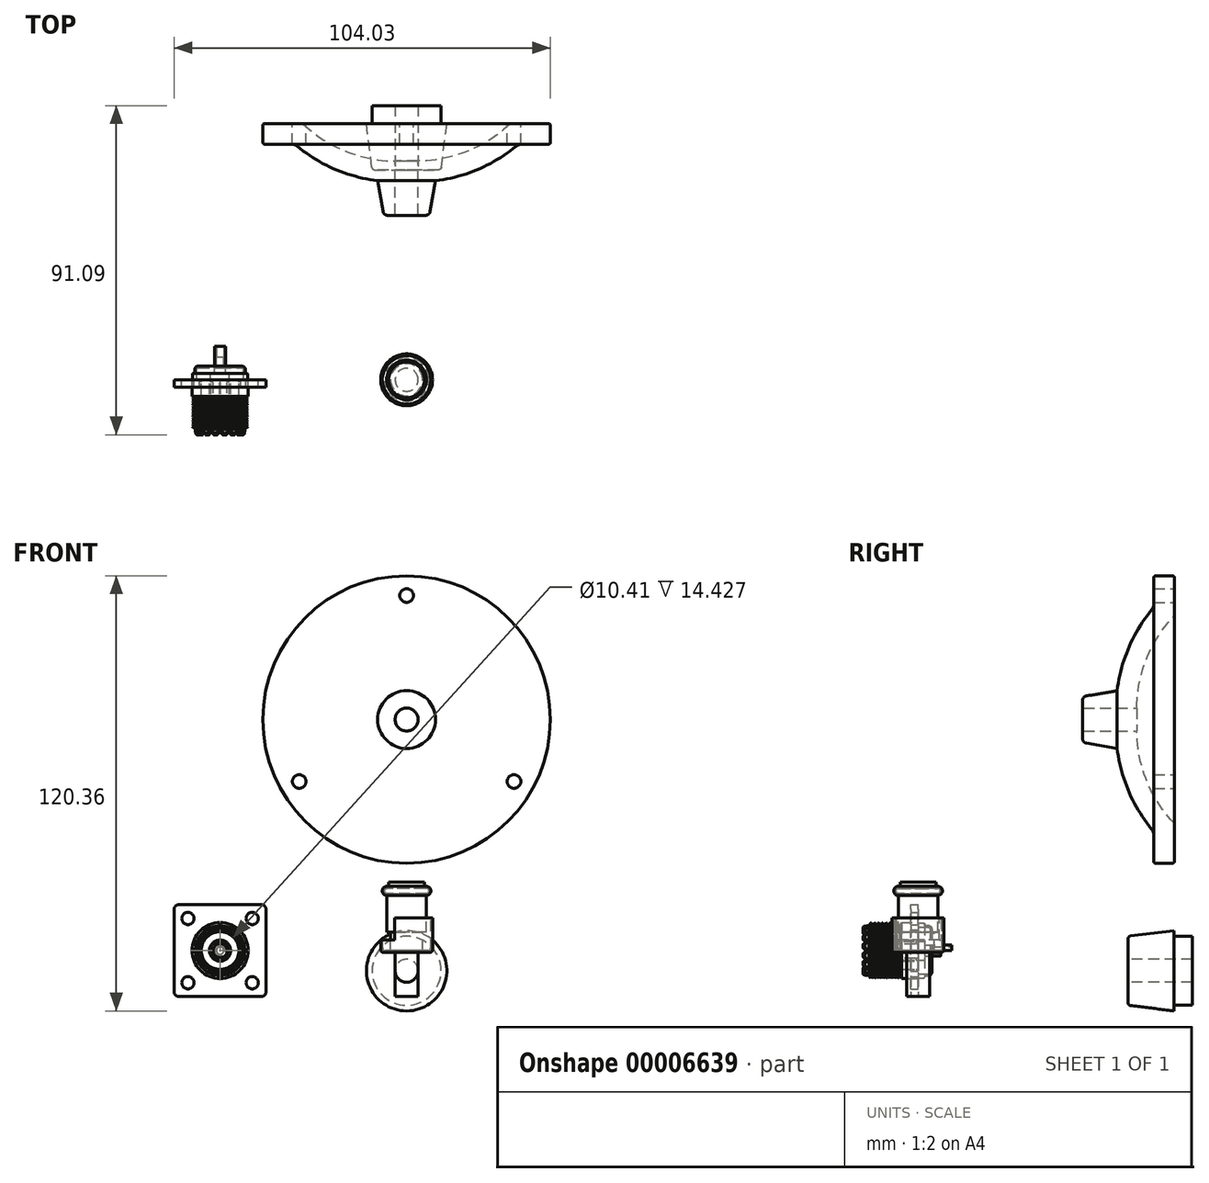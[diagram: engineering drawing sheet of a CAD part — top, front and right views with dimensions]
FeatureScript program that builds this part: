
annotation { "Feature Type Name" : "Feature", "Feature Type Description" : "" }
export const myFeature = defineFeature(function(context is Context, id is Id, definition is map)
    precondition{}
    {
        {
            var Q0;
            Q0=qCreatedBy(makeId("Right.planeOp"),FACE);
            var sketch = newSketch(context, id + "F0", { "sketchPlane" : qUnion([Q0])});
            skLineSegment(sketch, "E0", {"start": v(70.89, 103.16) * mm, "end": v(70.89, 92.87) * mm});
            skLineSegment(sketch, "E1", {"start": v(65.17, 103.16) * mm, "end": v(65.17, 84.88) * mm});
            skLineSegment(sketch, "E2", {"start": v(69.81, 63.92) * mm, "end": v(49.64, 63.92) * mm, "construction": true});
            skLineSegment(sketch, "E3", {"start": v(86.2, 94.9) * mm, "end": v(31.84, 94.9) * mm, "construction": true});
            skLineSegment(sketch, "E4", {"start": v(70.38, 103.67) * mm, "end": v(65.68, 103.67) * mm});
            skLineSegment(sketch, "E5", {"start": v(54.76, 115.1) * mm, "end": v(54.76, 52.48) * mm, "construction": true});
            skLineSegment(sketch, "E6", {"start": v(45.49, 106.52) * mm, "end": v(45.49, 54.26) * mm, "construction": true});
            skLineSegment(sketch, "E7", {"start": v(78.6, 71.85) * mm, "end": v(34.43, 71.85) * mm, "construction": true});
            skLineSegment(sketch, "E8", {"start": v(27.47, 70.27) * mm, "end": v(90.57, 70.27) * mm, "construction": true});
            skLineSegment(sketch, "E9", {"start": v(86.85, 67.1) * mm, "end": v(33.78, 67.1) * mm, "construction": true});
            skPoint(sketch, "E10.orphan", {"position": v(70.89, 63.92) * mm});
            skLineSegment(sketch, "E11", {"start": v(60.5, 67.1) * mm, "end": v(45.74, 67.1) * mm});
            skLineSegment(sketch, "E12", {"start": v(45.49, 67.34) * mm, "end": v(45.49, 69.2) * mm});
            skLineSegment(sketch, "E13", {"start": v(46.54, 70.45) * mm, "end": v(55.07, 71.9) * mm});
            skArc(sketch, "E14", {"start": v(65.17, 94.9) * mm, "mid": v(58.4, 84.13) * mm, "end": v(55.06, 71.85) * mm});
            skArc(sketch, "E15.0", {"start": v(70.75, 92.52) * mm, "mid": v(63.21, 80.75) * mm, "end": v(60.5, 67.04) * mm});
            skPoint(sketch, "E16.visualSharp", {"position": v(70.89, 103.67) * mm});
            skArc(sketch, "E16.filletArc", {"start": v(70.89, 103.16) * mm, "mid": v(70.74, 103.52) * mm, "end": v(70.38, 103.67) * mm});
            skPoint(sketch, "E17.visualSharp", {"position": v(65.17, 103.67) * mm});
            skArc(sketch, "E17.filletArc", {"start": v(65.68, 103.67) * mm, "mid": v(65.32, 103.52) * mm, "end": v(65.17, 103.16) * mm});
            skPoint(sketch, "E18.visualSharp", {"position": v(70.89, 92.67) * mm});
            skArc(sketch, "E18.filletArc", {"start": v(70.75, 92.52) * mm, "mid": v(70.85, 92.68) * mm, "end": v(70.89, 92.87) * mm});
            skPoint(sketch, "E19.visualSharp", {"position": v(45.49, 70.27) * mm});
            skArc(sketch, "E19.filletArc", {"start": v(46.54, 70.45) * mm, "mid": v(45.79, 70.01) * mm, "end": v(45.49, 69.2) * mm});
            skPoint(sketch, "E20.visualSharp", {"position": v(45.49, 67.1) * mm});
            skArc(sketch, "E20.filletArc", {"start": v(45.49, 67.34) * mm, "mid": v(45.56, 67.17) * mm, "end": v(45.74, 67.1) * mm});
            skLineSegment(sketch, "E21", {"start": v(43.2, -5.58) * mm, "end": v(88.96, -5.58) * mm, "construction": true});
            skLineSegment(sketch, "E22", {"start": v(70.77, -33.7) * mm, "end": v(70.77, 20.3) * mm, "construction": true});
            skLineSegment(sketch, "E23", {"start": v(75.85, -2.4) * mm, "end": v(58.07, -2.4) * mm});
            skLineSegment(sketch, "E24", {"start": v(58.07, -2.4) * mm, "end": v(58.07, 3.27) * mm});
            skLineSegment(sketch, "E25", {"start": v(58.74, 4.03) * mm, "end": v(70.77, 5.53) * mm});
            skLineSegment(sketch, "E26", {"start": v(70.77, 5.53) * mm, "end": v(70.77, 3.95) * mm});
            skLineSegment(sketch, "E27", {"start": v(70.77, 3.95) * mm, "end": v(75.85, 3.95) * mm});
            skLineSegment(sketch, "E28", {"start": v(75.85, 3.95) * mm, "end": v(75.85, -2.4) * mm});
            skPoint(sketch, "E29.visualSharp", {"position": v(58.07, 3.95) * mm});
            skArc(sketch, "E29.filletArc", {"start": v(58.74, 4.03) * mm, "mid": v(58.26, 3.78) * mm, "end": v(58.07, 3.27) * mm});
            skSolve(sketch);
        }
        {
            var Q0;
            Q0=makeQuery(id+"F0.imprint","IMPRINT",FACE,{"disambiguationData":[TD([[makeQuery(id+"F0.imprint","IMPRINT",EDGE,{"derivedFrom":sQuery(id+"F0.wireOp",EDGE,"E0")}),-1.0]])]});
            var Q1;
            {var subQ1=sQuery(id+"F0.wireOp",EDGE,"E11");Q1=makeQuery(id+"F0.imprint","IMPRINT",FACE,{"disambiguationData":[TD([[makeQuery(id+"F0.imprint","IMPRINT",EDGE,{"derivedFrom":subQ1}),-1.0]])]});}
            var Q2;
            Q2=sQuery(id+"F0.wireOp",EDGE,"E2");
            revolve(context, id + "F1", {"entities" : qUnion([Q0, Q1]), "axis" : qUnion([Q2]), "revolveType" : RevolveType.FULL});
        }
        {
            var Q0;
            Q0=makeQuery(id+"F1.opRevolve","SWEPT_EDGE",EDGE,{"disambiguationData":[OSD([sQuery(id+"F0.wireOp",EDGE,"E1"),sQuery(id+"F0.wireOp",EDGE,"E14")])]});
            fillet(context, id + "F2", {"entities" : qUnion([Q0]), "radius" : 2.54 * mm, "tangentPropagation" : true, "allowEdgeOverflow" : false});
        }
        {
            var Q0;
            Q0=makeQuery(id+"F1.opRevolve","SWEPT_FACE",FACE,{"disambiguationData":[OSD([sQuery(id+"F0.wireOp",EDGE,"E0")])]});
            var sketch = newSketch(context, id + "F3", { "sketchPlane" : qUnion([Q0])});
            skLineSegment(sketch, "E30", {"start": v(0, 63.92) * mm, "end": v(0, 114.75) * mm, "construction": true});
            skLineSegment(sketch, "E31", {"start": v(-51.87, 98.2) * mm, "end": v(47.7, 98.2) * mm, "construction": true});
            skCircle(sketch, "E32", {"center": v(0, 98.2) * mm, "radius": 1.9 * mm});
            skCircle(sketch, "E33.1.0", {"center": v(-29.7, 46.77) * mm, "radius": 1.9 * mm});
            skCircle(sketch, "E33.2.0", {"center": v(29.7, 46.77) * mm, "radius": 1.9 * mm});
            skPoint(sketch, "E33.center", {"position": v(0, 63.92) * mm});
            skSolve(sketch);
        }
        {
            var Q0;
            Q0=makeQuery(id+"F3.imprint","IMPRINT",FACE,{"disambiguationData":[TD([[makeQuery(id+"F3.imprint","IMPRINT",EDGE,{"derivedFrom":sQuery(id+"F3.wireOp",EDGE,"E32")}),1.0]])]});
            var Q1;
            Q1=makeQuery(id+"F3.imprint","IMPRINT",FACE,{"disambiguationData":[TD([[makeQuery(id+"F3.imprint","IMPRINT",EDGE,{"derivedFrom":sQuery(id+"F3.wireOp",EDGE,"E33.1.0")}),1.0]])]});
            var Q2;
            Q2=makeQuery(id+"F3.imprint","IMPRINT",FACE,{"disambiguationData":[TD([[makeQuery(id+"F3.imprint","IMPRINT",EDGE,{"derivedFrom":sQuery(id+"F3.wireOp",EDGE,"E33.2.0")}),1.0]])]});
            extrude(context, id + "F4", {"entities" : qUnion([Q0, Q1, Q2]), "operationType" : NewBodyOperationType.REMOVE, "oppositeDirection" : true, "depth" : 7.62 * mm});
        }
        {
            var Q0;
            Q0=makeQuery(id+"F0.imprint","IMPRINT",FACE,{"disambiguationData":[TD([[makeQuery(id+"F0.imprint","IMPRINT",EDGE,{"derivedFrom":sQuery(id+"F0.wireOp",EDGE,"E23")}),-1.0]])]});
            var Q1;
            Q1=sQuery(id+"F0.wireOp",EDGE,"E21");
            revolve(context, id + "F5", {"entities" : qUnion([Q0]), "axis" : qUnion([Q1]), "revolveType" : RevolveType.FULL});
        }
        {
            var Q0;
            Q0=qCreatedBy(makeId("Front.planeOp"),FACE);
            var sketch = newSketch(context, id + "F6", { "sketchPlane" : qUnion([Q0])});
            skLineSegment(sketch, "E34", {"start": v(0, 28.18) * mm, "end": v(0, -27.63) * mm, "construction": true});
            skLineSegment(sketch, "E35", {"start": v(-26.24, 0) * mm, "end": v(35.13, 0) * mm, "construction": true});
            skLineSegment(sketch, "E36", {"start": v(3.18, -12.7) * mm, "end": v(3.18, 0) * mm});
            skLineSegment(sketch, "E37", {"start": v(3.18, 0) * mm, "end": v(4.45, 0) * mm});
            skLineSegment(sketch, "E38", {"start": v(4.45, 0) * mm, "end": v(4.45, 5.08) * mm});
            skLineSegment(sketch, "E39", {"start": v(4.45, 5.08) * mm, "end": v(5.46, 5.08) * mm});
            skLineSegment(sketch, "E40", {"start": v(5.46, 5.08) * mm, "end": v(5.46, 15.24) * mm});
            skLineSegment(sketch, "E41", {"start": v(3.18, -12.7) * mm, "end": v(0, -12.7) * mm});
            skArc(sketch, "E42", {"start": v(5.46, 15.24) * mm, "mid": v(6.73, 16.51) * mm, "end": v(5.46, 17.78) * mm});
            skLineSegment(sketch, "E43", {"start": v(5.46, 17.78) * mm, "end": v(5.46, 17.22) * mm});
            skArc(sketch, "E44", {"start": v(5.44, 15.8) * mm, "mid": v(6.18, 16.5) * mm, "end": v(5.46, 17.22) * mm});
            skLineSegment(sketch, "E45", {"start": v(5.48, 15.8) * mm, "end": v(0, 15.8) * mm});
            skLineSegment(sketch, "E46", {"start": v(0, 15.8) * mm, "end": v(0, -12.7) * mm});
            skPoint(sketch, "E47.orphan", {"position": v(5.46, 18.14) * mm});
            skLineSegment(sketch, "E48", {"start": v(4.95, 18.92) * mm, "end": v(4.95, 17.22) * mm});
            skLineSegment(sketch, "E49", {"start": v(5.46, 17.22) * mm, "end": v(4.95, 17.22) * mm});
            skLineSegment(sketch, "E50", {"start": v(0, 17.22) * mm, "end": v(0, 15.8) * mm});
            skLineSegment(sketch, "E51", {"start": v(4.95, 18.92) * mm, "end": v(0, 18.92) * mm});
            skLineSegment(sketch, "E52", {"start": v(0, 18.92) * mm, "end": v(0, 17.22) * mm});
            skLineSegment(sketch, "E53", {"start": v(3.18, 0) * mm, "end": v(5.9, 0) * mm});
            skLineSegment(sketch, "E54", {"start": v(6.67, 0.76) * mm, "end": v(6.67, 9.02) * mm});
            skLineSegment(sketch, "E55", {"start": v(6.67, 9.02) * mm, "end": v(7.18, 9.02) * mm});
            skLineSegment(sketch, "E56", {"start": v(7.18, 9.02) * mm, "end": v(7.18, 0.25) * mm});
            skLineSegment(sketch, "E57", {"start": v(6.41, -0.5) * mm, "end": v(3.18, -0.5) * mm});
            skLineSegment(sketch, "E58", {"start": v(3.18, -0.5) * mm, "end": v(3.18, 0) * mm});
            skPoint(sketch, "E59.visualSharp", {"position": v(6.67, 0) * mm});
            skArc(sketch, "E59.filletArc", {"start": v(5.9, 0) * mm, "mid": v(6.44, 0.22) * mm, "end": v(6.67, 0.76) * mm});
            skPoint(sketch, "E60.visualSharp", {"position": v(7.18, -0.5) * mm});
            skArc(sketch, "E60.filletArc", {"start": v(6.41, -0.5) * mm, "mid": v(6.95, -0.28) * mm, "end": v(7.18, 0.25) * mm});
            skLineSegment(sketch, "E61.top", {"start": v(6.67, 2.92) * mm, "end": v(7.18, 2.92) * mm});
            skSolve(sketch);
        }
        {
            var Q0;
            Q0=makeQuery(id+"F6.imprint","IMPRINT",FACE,{"disambiguationData":[TD([[makeQuery(id+"F6.imprint","IMPRINT",EDGE,{"derivedFrom":sQuery(id+"F6.wireOp",EDGE,"E36")}),1.0]])]});
            var Q1;
            Q1=sQuery(id+"F6.wireOp",EDGE,"E34");
            revolve(context, id + "F7", {"entities" : qUnion([Q0]), "axis" : qUnion([Q1]), "revolveType" : RevolveType.FULL});
        }
        {
            var Q0;
            Q0=makeQuery(id+"F6.imprint","IMPRINT",FACE,{"disambiguationData":[TD([[makeQuery(id+"F6.imprint","IMPRINT",EDGE,{"derivedFrom":sQuery(id+"F6.wireOp",EDGE,"E48")}),-1.0]])]});
            var Q1;
            Q1=sQuery(id+"F6.wireOp",EDGE,"E46");
            revolve(context, id + "F8", {"entities" : qUnion([Q0]), "axis" : qUnion([Q1]), "revolveType" : RevolveType.FULL});
        }
        {
            var Q0;
            Q0=makeQuery(id+"F6.imprint","IMPRINT",FACE,{"disambiguationData":[TD([[makeQuery(id+"F6.imprint","IMPRINT",EDGE,{"derivedFrom":sQuery(id+"F6.wireOp",EDGE,"E57")}),-1.0]])]});
            var Q1;
            Q1=sQuery(id+"F6.wireOp",EDGE,"E46");
            revolve(context, id + "F9", {"entities" : qUnion([Q0]), "axis" : qUnion([Q1]), "revolveType" : RevolveType.FULL});
        }
        {
            var Q0;
            {var subQ2=sQuery(id+"F6.wireOp",EDGE,"E55");Q0=makeQuery(id+"F6.imprint","IMPRINT",FACE,{"disambiguationData":[TD([[makeQuery(id+"F6.imprint","IMPRINT",EDGE,{"derivedFrom":subQ2}),-1.0]])]});}
            var Q1;
            Q1=sQuery(id+"F6.wireOp",EDGE,"E46");
            revolve(context, id + "F10", {"operationType" : NewBodyOperationType.ADD, "entities" : qUnion([Q0]), "axis" : qUnion([Q1]), "revolveType" : RevolveType.SYMMETRIC, "angle" : 234.39 * degree});
        }
        {
            var Q0;
            Q0=qCreatedBy(makeId("Front.planeOp"),FACE);
            var sketch = newSketch(context, id + "F11", { "sketchPlane" : qUnion([Q0])});
            skLineSegment(sketch, "E62", {"start": v(-51.58, -5.6) * mm, "end": v(-51.58, -62.4) * mm, "construction": true});
            skLineSegment(sketch, "E63", {"start": v(-88, 0) * mm, "end": v(-10.84, 0) * mm, "construction": true});
            skLineSegment(sketch, "E64.rect.bottom", {"start": v(-40.15, 12.7) * mm, "end": v(-63, 12.7) * mm});
            skLineSegment(sketch, "E64.rect.top", {"start": v(-40.15, -12.7) * mm, "end": v(-63, -12.7) * mm});
            skLineSegment(sketch, "E64.rect.left", {"start": v(-38.88, 11.43) * mm, "end": v(-38.88, -11.43) * mm});
            skLineSegment(sketch, "E64.rect.right", {"start": v(-64.28, 11.43) * mm, "end": v(-64.28, -11.43) * mm});
            skPoint(sketch, "E64.rect.middle", {"position": v(-51.58, 0) * mm});
            skCircle(sketch, "E65", {"center": v(-42.69, 8.9) * mm, "radius": 1.71 * mm});
            skCircle(sketch, "E66", {"center": v(-51.58, 0) * mm, "radius": 5.72 * mm});
            skCircle(sketch, "E67.0.1.0", {"center": v(-42.69, -8.9) * mm, "radius": 1.71 * mm});
            skCircle(sketch, "E67.1.0.0", {"center": v(-60.47, 8.9) * mm, "radius": 1.71 * mm});
            skCircle(sketch, "E67.1.1.0", {"center": v(-60.47, -8.9) * mm, "radius": 1.71 * mm});
            skLineSegment(sketch, "E67.direction1", {"start": v(-42.69, 8.9) * mm, "end": v(-60.47, 8.9) * mm, "construction": true});
            skLineSegment(sketch, "E67.direction2", {"start": v(-42.69, 8.9) * mm, "end": v(-42.69, -8.9) * mm, "construction": true});
            skPoint(sketch, "E68.visualSharp", {"position": v(-64.28, 12.7) * mm});
            skArc(sketch, "E68.filletArc", {"start": v(-63, 12.7) * mm, "mid": v(-63.9, 12.33) * mm, "end": v(-64.28, 11.43) * mm});
            skPoint(sketch, "E69.visualSharp", {"position": v(-38.88, 12.7) * mm});
            skArc(sketch, "E69.filletArc", {"start": v(-38.88, 11.43) * mm, "mid": v(-39.25, 12.33) * mm, "end": v(-40.15, 12.7) * mm});
            skPoint(sketch, "E70.visualSharp", {"position": v(-38.88, -12.7) * mm});
            skArc(sketch, "E70.filletArc", {"start": v(-40.15, -12.7) * mm, "mid": v(-39.25, -12.33) * mm, "end": v(-38.88, -11.43) * mm});
            skPoint(sketch, "E71.visualSharp", {"position": v(-64.28, -12.7) * mm});
            skArc(sketch, "E71.filletArc", {"start": v(-64.28, -11.43) * mm, "mid": v(-63.9, -12.33) * mm, "end": v(-63, -12.7) * mm});
            skSolve(sketch);
        }
        {
            var Q0;
            Q0=makeQuery(id+"F11.imprint","IMPRINT",FACE,{"disambiguationData":[TD([[makeQuery(id+"F11.imprint","IMPRINT",EDGE,{"derivedFrom":sQuery(id+"F11.wireOp",EDGE,"E64.rect.bottom")}),1.0]])]});
            extrude(context, id + "F12", {"entities" : qUnion([Q0]), "depth" : 2.03 * mm});
        }
        {
            var Q0;
            Q0=makeQuery(id+"F12.opExtrude","SWEPT_FACE",FACE,{"disambiguationData":[OSD([sQuery(id+"F11.wireOp",EDGE,"E64.rect.right")])]});
            cPlane(context, id + "F13", {"entities" : qUnion([Q0]), "cplaneType" : CPlaneType.OFFSET, "offset" : 12.7 * mm, "oppositeDirection" : true, "width" : 152.4 * mm, "height" : 152.4 * mm});
        }
        {
            var Q0;
            Q0=qCreatedBy(id+"F13.planeOp",FACE);
            var sketch = newSketch(context, id + "F14", { "sketchPlane" : qUnion([Q0])});
            skLineSegment(sketch, "E72", {"start": v(-17.89, 0) * mm, "end": v(22.08, 0) * mm, "construction": true});
            skLineSegment(sketch, "E73", {"start": v(0, 5.2) * mm, "end": v(15.24, 5.2) * mm});
            skLineSegment(sketch, "E74", {"start": v(15.24, 5.2) * mm, "end": v(15.24, 6.83) * mm});
            skLineSegment(sketch, "E75", {"start": v(15.24, 6.83) * mm, "end": v(13.57, 6.83) * mm});
            skLineSegment(sketch, "E76", {"start": v(4.57, 7.75) * mm, "end": v(0, 7.75) * mm});
            skLineSegment(sketch, "E77", {"start": v(2.03, 15.2) * mm, "end": v(2.03, -14.59) * mm, "construction": true});
            skLineSegment(sketch, "E78", {"start": v(-0.58, 7.62) * mm, "end": v(-1.52, 7.62) * mm});
            skLineSegment(sketch, "E79", {"start": v(-2.03, 6.99) * mm, "end": v(-2.8, 6.99) * mm});
            skLineSegment(sketch, "E80", {"start": v(-1.03, 5.97) * mm, "end": v(-7.37, 5.97) * mm, "construction": true});
            skLineSegment(sketch, "E81", {"start": v(-0.58, 7.62) * mm, "end": v(0, 7.62) * mm});
            skLineSegment(sketch, "E82", {"start": v(0, 7.75) * mm, "end": v(0, 7.62) * mm});
            skLineSegment(sketch, "E83", {"start": v(-1.78, 7.37) * mm, "end": v(-1.78, 7.24) * mm});
            skPoint(sketch, "E84.orphan", {"position": v(-1.78, 7.62) * mm});
            skLineSegment(sketch, "E85", {"start": v(-3.81, 9.49) * mm, "end": v(-3.8, -2.76) * mm, "construction": true});
            skPoint(sketch, "E86", {"position": v(-3.81, 5.97) * mm});
            skArc(sketch, "E87", {"start": v(-2.8, 6.99) * mm, "mid": v(-3.51, 6.69) * mm, "end": v(-3.81, 5.97) * mm});
            skPoint(sketch, "E88.orphan", {"position": v(-2.8, 6.99) * mm});
            skArc(sketch, "E89.filletArc", {"start": v(-1.52, 7.62) * mm, "mid": v(-1.7, 7.55) * mm, "end": v(-1.78, 7.37) * mm});
            skPoint(sketch, "E90.visualSharp", {"position": v(-1.78, 6.99) * mm});
            skArc(sketch, "E90.filletArc", {"start": v(-2.03, 6.99) * mm, "mid": v(-1.85, 7.06) * mm, "end": v(-1.78, 7.24) * mm});
            skArc(sketch, "E91", {"start": v(-2.8, 6.48) * mm, "mid": v(-3.15, 6.33) * mm, "end": v(-3.3, 5.97) * mm});
            skLineSegment(sketch, "E92", {"start": v(-3.81, 5.97) * mm, "end": v(-3.3, 5.97) * mm});
            skLineSegment(sketch, "E93", {"start": v(-2.8, 6.48) * mm, "end": v(0, 6.48) * mm});
            skLineSegment(sketch, "E94", {"start": v(0, 6.48) * mm, "end": v(0, 5.2) * mm});
            skLineSegment(sketch, "E95", {"start": v(-1.78, 1.52) * mm, "end": v(-9.27, 1.52) * mm});
            skLineSegment(sketch, "E96", {"start": v(-9.27, 1.52) * mm, "end": v(-9.27, 1.02) * mm});
            skLineSegment(sketch, "E97", {"start": v(-9.27, 1.02) * mm, "end": v(-3.81, 1.02) * mm});
            skLineSegment(sketch, "E98", {"start": v(-3.81, 1.02) * mm, "end": v(-3.81, 0) * mm});
            skLineSegment(sketch, "E99", {"start": v(0, 2.6) * mm, "end": v(13.2, 2.6) * mm});
            skLineSegment(sketch, "E100", {"start": v(13.2, 2.6) * mm, "end": v(13.2, 1.97) * mm});
            skLineSegment(sketch, "E101", {"start": v(13.2, 1.97) * mm, "end": v(0, 1.97) * mm});
            skLineSegment(sketch, "E102", {"start": v(0, 1.97) * mm, "end": v(0, 0) * mm});
            skLineSegment(sketch, "E103", {"start": v(0, 2.6) * mm, "end": v(-1.78, 2.6) * mm});
            skLineSegment(sketch, "E104", {"start": v(-1.78, 2.6) * mm, "end": v(-1.78, 1.52) * mm});
            skLineSegment(sketch, "E105", {"start": v(-3.81, 0) * mm, "end": v(0, 0) * mm});
            skLineSegment(sketch, "E106", {"start": v(-3.81, 5.97) * mm, "end": v(-3.81, 1.52) * mm});
            skLineSegment(sketch, "E107", {"start": v(0, 2.92) * mm, "end": v(13.2, 2.92) * mm});
            skLineSegment(sketch, "E108", {"start": v(13.2, 2.92) * mm, "end": v(13.2, 5.2) * mm});
            skLineSegment(sketch, "E109", {"start": v(0, 2.6) * mm, "end": v(0, 2.92) * mm});
            skPoint(sketch, "E110.orphan", {"position": v(0.8, 2.92) * mm});
            skLineSegment(sketch, "E111", {"start": v(13.72, 9.23) * mm, "end": v(13.72, 6.12) * mm, "construction": true});
            skLineSegment(sketch, "E112", {"start": v(4.57, 7.75) * mm, "end": v(5.1, 6.83) * mm});
            skLineSegment(sketch, "E113", {"start": v(5.1, 6.83) * mm, "end": v(5.63, 7.75) * mm});
            skLineSegment(sketch, "E114", {"start": v(5.63, 7.75) * mm, "end": v(6.16, 6.83) * mm});
            skLineSegment(sketch, "E115.1.0.0", {"start": v(6.16, 6.83) * mm, "end": v(6.69, 7.75) * mm});
            skLineSegment(sketch, "E115.1.0.1", {"start": v(6.69, 7.75) * mm, "end": v(7.22, 6.83) * mm});
            skLineSegment(sketch, "E115.2.0.0", {"start": v(7.22, 6.83) * mm, "end": v(7.75, 7.75) * mm});
            skLineSegment(sketch, "E115.2.0.1", {"start": v(7.75, 7.75) * mm, "end": v(8.28, 6.83) * mm});
            skLineSegment(sketch, "E115.3.0.0", {"start": v(8.28, 6.83) * mm, "end": v(8.8, 7.75) * mm});
            skLineSegment(sketch, "E115.3.0.1", {"start": v(8.8, 7.75) * mm, "end": v(9.33, 6.83) * mm});
            skLineSegment(sketch, "E115.4.0.0", {"start": v(9.33, 6.83) * mm, "end": v(9.86, 7.75) * mm});
            skLineSegment(sketch, "E115.4.0.1", {"start": v(9.86, 7.75) * mm, "end": v(10.4, 6.83) * mm});
            skLineSegment(sketch, "E115.5.0.0", {"start": v(10.4, 6.83) * mm, "end": v(10.92, 7.75) * mm});
            skLineSegment(sketch, "E115.5.0.1", {"start": v(10.92, 7.75) * mm, "end": v(11.45, 6.83) * mm});
            skLineSegment(sketch, "E115.6.0.0", {"start": v(11.45, 6.83) * mm, "end": v(11.98, 7.75) * mm});
            skLineSegment(sketch, "E115.6.0.1", {"start": v(11.98, 7.75) * mm, "end": v(12.5, 6.83) * mm});
            skLineSegment(sketch, "E115.7.0.0", {"start": v(12.5, 6.83) * mm, "end": v(13.04, 7.75) * mm});
            skLineSegment(sketch, "E115.7.0.1", {"start": v(13.04, 7.75) * mm, "end": v(13.57, 6.83) * mm});
            skLineSegment(sketch, "E115.direction1", {"start": v(5.1, 6.83) * mm, "end": v(6.16, 6.83) * mm, "construction": true});
            skLineSegment(sketch, "E116", {"start": v(-6.22, 1.52) * mm, "end": v(-6.22, 1.02) * mm});
            skSolve(sketch);
        }
        {
            var Q0;
            {var subQ3=sQuery(id+"F14.wireOp",EDGE,"E74");Q0=makeQuery(id+"F14.imprint","IMPRINT",FACE,{"disambiguationData":[TD([[makeQuery(id+"F14.imprint","IMPRINT",EDGE,{"derivedFrom":subQ3}),1.0]])]});}
            var Q1;
            Q1=sQuery(id+"F14.wireOp",EDGE,"E72");
            revolve(context, id + "F15", {"entities" : qUnion([Q0]), "axis" : qUnion([Q1]), "revolveType" : RevolveType.FULL});
        }
        {
            var Q0;
            Q0=makeQuery(id+"F14.imprint","IMPRINT",FACE,{"disambiguationData":[TD([[makeQuery(id+"F14.imprint","IMPRINT",EDGE,{"derivedFrom":sQuery(id+"F14.wireOp",EDGE,"E91")}),1.0]])]});
            var Q1;
            Q1=sQuery(id+"F14.wireOp",EDGE,"E72");
            revolve(context, id + "F16", {"entities" : qUnion([Q0]), "axis" : qUnion([Q1]), "revolveType" : RevolveType.FULL});
        }
        {
            var Q0;
            {var subQ3=sQuery(id+"F14.wireOp",EDGE,"E98");Q0=makeQuery(id+"F14.imprint","IMPRINT",FACE,{"disambiguationData":[TD([[makeQuery(id+"F14.imprint","IMPRINT",EDGE,{"derivedFrom":subQ3}),1.0]])]});}
            var Q1;
            Q1=sQuery(id+"F14.wireOp",EDGE,"E72");
            revolve(context, id + "F17", {"entities" : qUnion([Q0]), "axis" : qUnion([Q1]), "revolveType" : RevolveType.FULL});
        }
        {
            var Q0;
            {var subQ2=sQuery(id+"F14.wireOp",EDGE,"E96");Q0=makeQuery(id+"F14.imprint","IMPRINT",FACE,{"disambiguationData":[TD([[makeQuery(id+"F14.imprint","IMPRINT",EDGE,{"derivedFrom":subQ2}),1.0]])]});}
            var Q1;
            Q1=sQuery(id+"F14.wireOp",EDGE,"E72");
            revolve(context, id + "F18", {"operationType" : NewBodyOperationType.ADD, "entities" : qUnion([Q0]), "axis" : qUnion([Q1]), "revolveType" : RevolveType.SYMMETRIC, "angle" : 180 * degree});
        }
        {
            var Q0;
            Q0=makeQuery(id+"F17.opRevolve","SWEPT_EDGE",EDGE,{"disambiguationData":[OSD([sQuery(id+"F14.wireOp",EDGE,"E100"),sQuery(id+"F14.wireOp",EDGE,"E101")])]});
            fillet(context, id + "F19", {"entities" : qUnion([Q0]), "radius" : 0.25 * mm, "tangentPropagation" : true, "allowEdgeOverflow" : false});
        }
        {
            var Q0;
            Q0=makeQuery(id+"F17.opRevolve","SWEPT_FACE",FACE,{"disambiguationData":[OSD([sQuery(id+"F14.wireOp",EDGE,"E100")])]});
            var sketch = newSketch(context, id + "F20", { "sketchPlane" : qUnion([Q0])});
            skLineSegment(sketch, "E117.rect.bottom", {"start": v(-54.22, -0.13) * mm, "end": v(-51.7, -0.13) * mm});
            skLineSegment(sketch, "E117.rect.top", {"start": v(-54.22, 0.13) * mm, "end": v(-51.7, 0.13) * mm});
            skLineSegment(sketch, "E117.rect.left", {"start": v(-54.22, -0.13) * mm, "end": v(-54.22, 0.13) * mm});
            skLineSegment(sketch, "E117.rect.right", {"start": v(-48.94, -0.13) * mm, "end": v(-48.94, 0.13) * mm});
            skPoint(sketch, "E117.rect.middle", {"position": v(-51.58, 0) * mm});
            skLineSegment(sketch, "E118.rect.bottom", {"start": v(-51.7, -2.64) * mm, "end": v(-51.45, -2.64) * mm});
            skLineSegment(sketch, "E118.rect.top", {"start": v(-51.7, 2.64) * mm, "end": v(-51.45, 2.64) * mm});
            skLineSegment(sketch, "E118.rect.left", {"start": v(-51.7, -2.64) * mm, "end": v(-51.7, -0.13) * mm});
            skLineSegment(sketch, "E118.rect.right", {"start": v(-51.45, -2.64) * mm, "end": v(-51.45, -0.13) * mm});
            skLineSegment(sketch, "E119.trimOffspring", {"start": v(-51.7, 0.13) * mm, "end": v(-51.7, 2.64) * mm});
            skLineSegment(sketch, "E120.trimOffspring", {"start": v(-51.45, 0.13) * mm, "end": v(-51.45, 2.64) * mm});
            skLineSegment(sketch, "E121.trimOffspring", {"start": v(-51.45, -0.13) * mm, "end": v(-48.94, -0.13) * mm});
            skLineSegment(sketch, "E122.trimOffspring", {"start": v(-51.45, 0.13) * mm, "end": v(-48.94, 0.13) * mm});
            skSolve(sketch);
        }
        {
            var Q0;
            {var subQ12=sQuery(id+"F20.wireOp",EDGE,"E118.rect.left");var subQ18=sQuery(id+"F20.wireOp",EDGE,"E117.rect.bottom");var subQ21=makeQuery(id+"F20.imprint","INTERSECT",VERTEX,{"derivedFrom":[subQ18,subQ12]});Q0=makeQuery(id+"F20.imprint","IMPRINT",FACE,{"disambiguationData":[TD([[makeQuery(id+"F20.imprint","IMPRINT",EDGE,{"disambiguationData":[TD([[subQ21,1.0]])],"derivedFrom":subQ18}),1.0]])]});}
            var Q1;
            {var subQ0=sQuery(id+"F14.wireOp",EDGE,"E100");var subQ4=sQuery(id+"F20.wireOp",EDGE,"E117.rect.bottom");var subQ6=makeQuery(id+"F17.opRevolve","SWEPT_EDGE",EDGE,{"disambiguationData":[OSD([sQuery(id+"F14.wireOp",EDGE,"E99"),subQ0])]});var subQ8=makeQuery(id+"F20.imprint","INTERSECT",VERTEX,{"derivedFrom":[subQ6,subQ4]});Q1=makeQuery(id+"F20.imprint","IMPRINT",FACE,{"disambiguationData":[TD([[makeQuery(id+"F20.imprint","IMPRINT",EDGE,{"disambiguationData":[TD([[subQ8,-1.0]])],"derivedFrom":subQ4}),1.0]])]});}
            var Q2;
            {var subQ0=sQuery(id+"F14.wireOp",EDGE,"E100");var subQ4=sQuery(id+"F20.wireOp",EDGE,"E118.rect.left");var subQ6=makeQuery(id+"F17.opRevolve","SWEPT_EDGE",EDGE,{"disambiguationData":[OSD([sQuery(id+"F14.wireOp",EDGE,"E99"),subQ0])]});var subQ8=makeQuery(id+"F20.imprint","INTERSECT",VERTEX,{"derivedFrom":[subQ6,subQ4]});Q2=makeQuery(id+"F20.imprint","IMPRINT",FACE,{"disambiguationData":[TD([[makeQuery(id+"F20.imprint","IMPRINT",EDGE,{"disambiguationData":[TD([[subQ8,-1.0]])],"derivedFrom":subQ4}),-1.0]])]});}
            var Q3;
            {var subQ0=sQuery(id+"F14.wireOp",EDGE,"E100");var subQ1=makeQuery(id+"F17.opRevolve","SWEPT_EDGE",EDGE,{"disambiguationData":[OSD([sQuery(id+"F14.wireOp",EDGE,"E99"),subQ0])]});var subQ4=sQuery(id+"F20.wireOp",EDGE,"E121.trimOffspring");var subQ5=makeQuery(id+"F20.imprint","INTERSECT",VERTEX,{"derivedFrom":[subQ1,subQ4]});Q3=makeQuery(id+"F20.imprint","IMPRINT",FACE,{"disambiguationData":[TD([[makeQuery(id+"F20.imprint","IMPRINT",EDGE,{"disambiguationData":[TD([[subQ5,1.0]])],"derivedFrom":subQ4}),1.0]])]});}
            var Q4;
            {var subQ0=sQuery(id+"F14.wireOp",EDGE,"E100");var subQ4=sQuery(id+"F20.wireOp",EDGE,"E119.trimOffspring");var subQ6=makeQuery(id+"F17.opRevolve","SWEPT_EDGE",EDGE,{"disambiguationData":[OSD([sQuery(id+"F14.wireOp",EDGE,"E99"),subQ0])]});var subQ8=makeQuery(id+"F20.imprint","INTERSECT",VERTEX,{"derivedFrom":[subQ6,subQ4]});Q4=makeQuery(id+"F20.imprint","IMPRINT",FACE,{"disambiguationData":[TD([[makeQuery(id+"F20.imprint","IMPRINT",EDGE,{"disambiguationData":[TD([[subQ8,1.0]])],"derivedFrom":subQ4}),-1.0]])]});}
            var Q5;
            {var subQ5=sQuery(id+"F20.wireOp",EDGE,"E118.rect.top");Q5=makeQuery(id+"F20.imprint","IMPRINT",FACE,{"disambiguationData":[TD([[makeQuery(id+"F20.imprint","IMPRINT",EDGE,{"derivedFrom":subQ5}),-1.0]])]});}
            var Q6;
            {var subQ5=sQuery(id+"F20.wireOp",EDGE,"E117.rect.left");Q6=makeQuery(id+"F20.imprint","IMPRINT",FACE,{"disambiguationData":[TD([[makeQuery(id+"F20.imprint","IMPRINT",EDGE,{"derivedFrom":subQ5}),-1.0]])]});}
            var Q7;
            {var subQ5=sQuery(id+"F20.wireOp",EDGE,"E118.rect.bottom");Q7=makeQuery(id+"F20.imprint","IMPRINT",FACE,{"disambiguationData":[TD([[makeQuery(id+"F20.imprint","IMPRINT",EDGE,{"derivedFrom":subQ5}),1.0]])]});}
            var Q8;
            {var subQ5=sQuery(id+"F20.wireOp",EDGE,"E117.rect.right");Q8=makeQuery(id+"F20.imprint","IMPRINT",FACE,{"disambiguationData":[TD([[makeQuery(id+"F20.imprint","IMPRINT",EDGE,{"derivedFrom":subQ5}),1.0]])]});}
            extrude(context, id + "F21", {"entities" : qUnion([Q0, Q1, Q2, Q3, Q4, Q5, Q6, Q7, Q8]), "operationType" : NewBodyOperationType.REMOVE, "oppositeDirection" : true, "depth" : 12.7 * mm});
        }
        {
            var Q0;
            Q0=makeQuery(id+"F15.opRevolve","SWEPT_FACE",FACE,{"disambiguationData":[OSD([sQuery(id+"F14.wireOp",EDGE,"E74")])]});
            var sketch = newSketch(context, id + "F22", { "sketchPlane" : qUnion([Q0])});
            skCircle(sketch, "E123", {"center": v(-51.58, 0) * mm, "radius": 5.78 * mm});
            skSolve(sketch);
        }
        {
            var Q0;
            Q0=makeQuery(id+"F22.imprint","IMPRINT",FACE,{"disambiguationData":[TD([[makeQuery(id+"F22.imprint","IMPRINT",EDGE,{"derivedFrom":sQuery(id+"F22.wireOp",EDGE,"E123")}),1.0]])]});
            extrude(context, id + "F23", {"entities" : qUnion([Q0]), "operationType" : NewBodyOperationType.REMOVE, "oppositeDirection" : true, "depth" : 0.81 * mm});
        }
        {
            var Q0;
            Q0=qCreatedBy(makeId("Top.planeOp"),FACE);
            var sketch = newSketch(context, id + "F24", { "sketchPlane" : qUnion([Q0])});
            skLineSegment(sketch, "E124", {"start": v(-58.76, -14.48) * mm, "end": v(-44.47, -14.48) * mm, "construction": true});
            skLineSegment(sketch, "E125", {"start": v(-44.53, -15.24) * mm, "end": v(-60.23, -15.24) * mm, "construction": true});
            skLineSegment(sketch, "E126", {"start": v(-51.62, -14.48) * mm, "end": v(-52.38, -15.24) * mm});
            skLineSegment(sketch, "E127", {"start": v(-51.62, -14.48) * mm, "end": v(-50.85, -15.24) * mm});
            skLineSegment(sketch, "E128", {"start": v(-52.38, -15.24) * mm, "end": v(-50.85, -15.24) * mm});
            skSolve(sketch);
        }
        {
            var Q0;
            Q0=makeQuery(id+"F24.imprint","IMPRINT",FACE,{"disambiguationData":[TD([[makeQuery(id+"F24.imprint","IMPRINT",EDGE,{"derivedFrom":sQuery(id+"F24.wireOp",EDGE,"E126")}),1.0]])]});
            extrude(context, id + "F25", {"entities" : qUnion([Q0]), "operationType" : NewBodyOperationType.REMOVE, "endBound" : BoundingType.SYMMETRIC, "oppositeDirection" : true, "depth" : 15.24 * mm});
        }
        {
            var Q0;
            Q0=makeQuery(id+"F25.boolean.opBoolean","COPY",FACE,{"disambiguationData":[OD(0.0)],"derivedFrom":makeQuery(id+"F25.opExtrude","SWEPT_FACE",FACE,{"disambiguationData":[OSD([sQuery(id+"F24.wireOp",EDGE,"E126")])]})});
            var Q1;
            Q1=makeQuery(id+"F25.boolean.opBoolean","COPY",FACE,{"disambiguationData":[OD(0.0)],"derivedFrom":makeQuery(id+"F25.opExtrude","SWEPT_FACE",FACE,{"disambiguationData":[OSD([sQuery(id+"F24.wireOp",EDGE,"E127")])]})});
            var Q2;
            Q2=makeQuery(id+"F25.boolean.opBoolean","COPY",FACE,{"disambiguationData":[OD(1.0)],"derivedFrom":makeQuery(id+"F25.opExtrude","SWEPT_FACE",FACE,{"disambiguationData":[OSD([sQuery(id+"F24.wireOp",EDGE,"E126")])]})});
            var Q3;
            Q3=makeQuery(id+"F25.boolean.opBoolean","COPY",FACE,{"disambiguationData":[OD(1.0)],"derivedFrom":makeQuery(id+"F25.opExtrude","SWEPT_FACE",FACE,{"disambiguationData":[OSD([sQuery(id+"F24.wireOp",EDGE,"E127")])]})});
            var Q4;
            Q4=sQuery(id+"F14.wireOp",EDGE,"E72");
            circularPattern(context, id + "F26", {"faces" : qUnion([Q0, Q1, Q2, Q3]), "axis" : qUnion([Q4]), "angle" : 22.5 * degree, "instanceCount" : 8, "patternType" : PatternType.FACE});
        }
        {
            var Q0;
            Q0=makeQuery(id+"F25.boolean.opBoolean","INTERSECT",EDGE,{"disambiguationData":[OD(1.0)],"derivedFrom":[makeQuery(id+"F23.boolean.opBoolean","COPY",FACE,{"derivedFrom":makeQuery(id+"F23.opExtrude","SWEPT_FACE",FACE,{"disambiguationData":[OSD([sQuery(id+"F22.wireOp",EDGE,"E123")])]})}),makeQuery(id+"F25.opExtrude","SWEPT_FACE",FACE,{"disambiguationData":[OSD([sQuery(id+"F24.wireOp",EDGE,"E126")])]})]});
            var Q1;
            {var subQ0=sQuery(id+"F22.wireOp",EDGE,"E123");Q1=makeQuery(id+"F26.opPattern","SPLIT",EDGE,{"disambiguationData":[OD(1.0)],"derivedFrom":makeQuery(id+"F25.boolean.opBoolean","SPLIT",EDGE,{"disambiguationData":[TD([makeQuery(id+"F25.opExtrude","SWEPT_FACE",FACE,{"disambiguationData":[OSD([sQuery(id+"F24.wireOp",EDGE,"E126")])]})])],"derivedFrom":makeQuery(id+"F23.boolean.opBoolean","COPY",EDGE,{"derivedFrom":makeQuery(id+"F23.opExtrude","CAP_EDGE",EDGE,{"disambiguationData":[OSD([subQ0])],"isStart":true})})})});}
            var Q2;
            Q2=makeQuery(id+"F26.opPattern","COPY",EDGE,{"derivedFrom":makeQuery(id+"F25.boolean.opBoolean","INTERSECT",EDGE,{"disambiguationData":[OD(1.0)],"derivedFrom":[makeQuery(id+"F23.boolean.opBoolean","COPY",FACE,{"derivedFrom":makeQuery(id+"F23.opExtrude","SWEPT_FACE",FACE,{"disambiguationData":[OSD([sQuery(id+"F22.wireOp",EDGE,"E123")])]})}),makeQuery(id+"F25.opExtrude","SWEPT_FACE",FACE,{"disambiguationData":[OSD([sQuery(id+"F24.wireOp",EDGE,"E127")])]})]}),"instanceName":"1"});
            var Q3;
            Q3=makeQuery(id+"F25.boolean.opBoolean","INTERSECT",EDGE,{"disambiguationData":[OD(1.0)],"derivedFrom":[makeQuery(id+"F23.boolean.opBoolean","COPY",FACE,{"derivedFrom":makeQuery(id+"F23.opExtrude","SWEPT_FACE",FACE,{"disambiguationData":[OSD([sQuery(id+"F22.wireOp",EDGE,"E123")])]})}),makeQuery(id+"F25.opExtrude","SWEPT_FACE",FACE,{"disambiguationData":[OSD([sQuery(id+"F24.wireOp",EDGE,"E127")])]})]});
            var Q4;
            {var subQ0=sQuery(id+"F22.wireOp",EDGE,"E123");Q4=makeQuery(id+"F26.opPattern","SPLIT",EDGE,{"disambiguationData":[OD(1.0)],"derivedFrom":makeQuery(id+"F25.boolean.opBoolean","SPLIT",EDGE,{"disambiguationData":[TD([makeQuery(id+"F25.opExtrude","SWEPT_FACE",FACE,{"disambiguationData":[OSD([sQuery(id+"F24.wireOp",EDGE,"E127")])]})])],"derivedFrom":makeQuery(id+"F23.boolean.opBoolean","COPY",EDGE,{"derivedFrom":makeQuery(id+"F23.opExtrude","CAP_EDGE",EDGE,{"disambiguationData":[OSD([subQ0])],"isStart":true})})})});}
            var Q5;
            Q5=makeQuery(id+"F26.opPattern","COPY",EDGE,{"derivedFrom":makeQuery(id+"F25.boolean.opBoolean","INTERSECT",EDGE,{"disambiguationData":[OD(0.0)],"derivedFrom":[makeQuery(id+"F23.boolean.opBoolean","COPY",FACE,{"derivedFrom":makeQuery(id+"F23.opExtrude","SWEPT_FACE",FACE,{"disambiguationData":[OSD([sQuery(id+"F22.wireOp",EDGE,"E123")])]})}),makeQuery(id+"F25.opExtrude","SWEPT_FACE",FACE,{"disambiguationData":[OSD([sQuery(id+"F24.wireOp",EDGE,"E127")])]})]}),"instanceName":"7"});
            var Q6;
            Q6=makeQuery(id+"F26.opPattern","COPY",EDGE,{"derivedFrom":makeQuery(id+"F25.boolean.opBoolean","INTERSECT",EDGE,{"disambiguationData":[OD(0.0)],"derivedFrom":[makeQuery(id+"F23.boolean.opBoolean","COPY",FACE,{"derivedFrom":makeQuery(id+"F23.opExtrude","SWEPT_FACE",FACE,{"disambiguationData":[OSD([sQuery(id+"F22.wireOp",EDGE,"E123")])]})}),makeQuery(id+"F25.opExtrude","SWEPT_FACE",FACE,{"disambiguationData":[OSD([sQuery(id+"F24.wireOp",EDGE,"E126")])]})]}),"instanceName":"7"});
            var Q7;
            {var subQ0=sQuery(id+"F22.wireOp",EDGE,"E123");Q7=makeQuery(id+"F26.opPattern","SPLIT",EDGE,{"disambiguationData":[OD(7.0)],"derivedFrom":makeQuery(id+"F25.boolean.opBoolean","SPLIT",EDGE,{"disambiguationData":[TD([makeQuery(id+"F25.opExtrude","SWEPT_FACE",FACE,{"disambiguationData":[OSD([sQuery(id+"F24.wireOp",EDGE,"E127")])]})])],"derivedFrom":makeQuery(id+"F23.boolean.opBoolean","COPY",EDGE,{"derivedFrom":makeQuery(id+"F23.opExtrude","CAP_EDGE",EDGE,{"disambiguationData":[OSD([subQ0])],"isStart":true})})})});}
            var Q8;
            Q8=makeQuery(id+"F26.opPattern","COPY",EDGE,{"derivedFrom":makeQuery(id+"F25.boolean.opBoolean","INTERSECT",EDGE,{"disambiguationData":[OD(0.0)],"derivedFrom":[makeQuery(id+"F23.boolean.opBoolean","COPY",FACE,{"derivedFrom":makeQuery(id+"F23.opExtrude","SWEPT_FACE",FACE,{"disambiguationData":[OSD([sQuery(id+"F22.wireOp",EDGE,"E123")])]})}),makeQuery(id+"F25.opExtrude","SWEPT_FACE",FACE,{"disambiguationData":[OSD([sQuery(id+"F24.wireOp",EDGE,"E127")])]})]}),"instanceName":"6"});
            var Q9;
            Q9=makeQuery(id+"F26.opPattern","COPY",EDGE,{"derivedFrom":makeQuery(id+"F25.boolean.opBoolean","INTERSECT",EDGE,{"disambiguationData":[OD(0.0)],"derivedFrom":[makeQuery(id+"F23.boolean.opBoolean","COPY",FACE,{"derivedFrom":makeQuery(id+"F23.opExtrude","SWEPT_FACE",FACE,{"disambiguationData":[OSD([sQuery(id+"F22.wireOp",EDGE,"E123")])]})}),makeQuery(id+"F25.opExtrude","SWEPT_FACE",FACE,{"disambiguationData":[OSD([sQuery(id+"F24.wireOp",EDGE,"E126")])]})]}),"instanceName":"6"});
            var Q10;
            {var subQ0=sQuery(id+"F22.wireOp",EDGE,"E123");Q10=makeQuery(id+"F26.opPattern","SPLIT",EDGE,{"disambiguationData":[OD(6.0)],"derivedFrom":makeQuery(id+"F25.boolean.opBoolean","SPLIT",EDGE,{"disambiguationData":[TD([makeQuery(id+"F25.opExtrude","SWEPT_FACE",FACE,{"disambiguationData":[OSD([sQuery(id+"F24.wireOp",EDGE,"E127")])]})])],"derivedFrom":makeQuery(id+"F23.boolean.opBoolean","COPY",EDGE,{"derivedFrom":makeQuery(id+"F23.opExtrude","CAP_EDGE",EDGE,{"disambiguationData":[OSD([subQ0])],"isStart":true})})})});}
            var Q11;
            Q11=makeQuery(id+"F26.opPattern","COPY",EDGE,{"derivedFrom":makeQuery(id+"F25.boolean.opBoolean","INTERSECT",EDGE,{"disambiguationData":[OD(0.0)],"derivedFrom":[makeQuery(id+"F23.boolean.opBoolean","COPY",FACE,{"derivedFrom":makeQuery(id+"F23.opExtrude","SWEPT_FACE",FACE,{"disambiguationData":[OSD([sQuery(id+"F22.wireOp",EDGE,"E123")])]})}),makeQuery(id+"F25.opExtrude","SWEPT_FACE",FACE,{"disambiguationData":[OSD([sQuery(id+"F24.wireOp",EDGE,"E127")])]})]}),"instanceName":"5"});
            var Q12;
            Q12=makeQuery(id+"F26.opPattern","COPY",EDGE,{"derivedFrom":makeQuery(id+"F25.boolean.opBoolean","INTERSECT",EDGE,{"disambiguationData":[OD(0.0)],"derivedFrom":[makeQuery(id+"F23.boolean.opBoolean","COPY",FACE,{"derivedFrom":makeQuery(id+"F23.opExtrude","SWEPT_FACE",FACE,{"disambiguationData":[OSD([sQuery(id+"F22.wireOp",EDGE,"E123")])]})}),makeQuery(id+"F25.opExtrude","SWEPT_FACE",FACE,{"disambiguationData":[OSD([sQuery(id+"F24.wireOp",EDGE,"E126")])]})]}),"instanceName":"5"});
            var Q13;
            Q13=makeQuery(id+"F26.opPattern","COPY",EDGE,{"derivedFrom":makeQuery(id+"F25.boolean.opBoolean","INTERSECT",EDGE,{"disambiguationData":[OD(0.0)],"derivedFrom":[makeQuery(id+"F23.boolean.opBoolean","COPY",FACE,{"derivedFrom":makeQuery(id+"F23.opExtrude","SWEPT_FACE",FACE,{"disambiguationData":[OSD([sQuery(id+"F22.wireOp",EDGE,"E123")])]})}),makeQuery(id+"F25.opExtrude","SWEPT_FACE",FACE,{"disambiguationData":[OSD([sQuery(id+"F24.wireOp",EDGE,"E127")])]})]}),"instanceName":"4"});
            var Q14;
            {var subQ0=sQuery(id+"F22.wireOp",EDGE,"E123");Q14=makeQuery(id+"F26.opPattern","SPLIT",EDGE,{"disambiguationData":[OD(5.0)],"derivedFrom":makeQuery(id+"F25.boolean.opBoolean","SPLIT",EDGE,{"disambiguationData":[TD([makeQuery(id+"F25.opExtrude","SWEPT_FACE",FACE,{"disambiguationData":[OSD([sQuery(id+"F24.wireOp",EDGE,"E127")])]})])],"derivedFrom":makeQuery(id+"F23.boolean.opBoolean","COPY",EDGE,{"derivedFrom":makeQuery(id+"F23.opExtrude","CAP_EDGE",EDGE,{"disambiguationData":[OSD([subQ0])],"isStart":true})})})});}
            var Q15;
            Q15=makeQuery(id+"F26.opPattern","COPY",EDGE,{"derivedFrom":makeQuery(id+"F25.boolean.opBoolean","INTERSECT",EDGE,{"disambiguationData":[OD(0.0)],"derivedFrom":[makeQuery(id+"F23.boolean.opBoolean","COPY",FACE,{"derivedFrom":makeQuery(id+"F23.opExtrude","SWEPT_FACE",FACE,{"disambiguationData":[OSD([sQuery(id+"F22.wireOp",EDGE,"E123")])]})}),makeQuery(id+"F25.opExtrude","SWEPT_FACE",FACE,{"disambiguationData":[OSD([sQuery(id+"F24.wireOp",EDGE,"E126")])]})]}),"instanceName":"4"});
            var Q16;
            {var subQ0=sQuery(id+"F22.wireOp",EDGE,"E123");Q16=makeQuery(id+"F26.opPattern","SPLIT",EDGE,{"disambiguationData":[OD(4.0)],"derivedFrom":makeQuery(id+"F25.boolean.opBoolean","SPLIT",EDGE,{"disambiguationData":[TD([makeQuery(id+"F25.opExtrude","SWEPT_FACE",FACE,{"disambiguationData":[OSD([sQuery(id+"F24.wireOp",EDGE,"E127")])]})])],"derivedFrom":makeQuery(id+"F23.boolean.opBoolean","COPY",EDGE,{"derivedFrom":makeQuery(id+"F23.opExtrude","CAP_EDGE",EDGE,{"disambiguationData":[OSD([subQ0])],"isStart":true})})})});}
            var Q17;
            Q17=makeQuery(id+"F26.opPattern","COPY",EDGE,{"derivedFrom":makeQuery(id+"F25.boolean.opBoolean","INTERSECT",EDGE,{"disambiguationData":[OD(0.0)],"derivedFrom":[makeQuery(id+"F23.boolean.opBoolean","COPY",FACE,{"derivedFrom":makeQuery(id+"F23.opExtrude","SWEPT_FACE",FACE,{"disambiguationData":[OSD([sQuery(id+"F22.wireOp",EDGE,"E123")])]})}),makeQuery(id+"F25.opExtrude","SWEPT_FACE",FACE,{"disambiguationData":[OSD([sQuery(id+"F24.wireOp",EDGE,"E127")])]})]}),"instanceName":"3"});
            var Q18;
            Q18=makeQuery(id+"F26.opPattern","COPY",EDGE,{"derivedFrom":makeQuery(id+"F25.boolean.opBoolean","INTERSECT",EDGE,{"disambiguationData":[OD(0.0)],"derivedFrom":[makeQuery(id+"F23.boolean.opBoolean","COPY",FACE,{"derivedFrom":makeQuery(id+"F23.opExtrude","SWEPT_FACE",FACE,{"disambiguationData":[OSD([sQuery(id+"F22.wireOp",EDGE,"E123")])]})}),makeQuery(id+"F25.opExtrude","SWEPT_FACE",FACE,{"disambiguationData":[OSD([sQuery(id+"F24.wireOp",EDGE,"E126")])]})]}),"instanceName":"3"});
            var Q19;
            {var subQ0=sQuery(id+"F22.wireOp",EDGE,"E123");Q19=makeQuery(id+"F26.opPattern","SPLIT",EDGE,{"disambiguationData":[OD(3.0)],"derivedFrom":makeQuery(id+"F25.boolean.opBoolean","SPLIT",EDGE,{"disambiguationData":[TD([makeQuery(id+"F25.opExtrude","SWEPT_FACE",FACE,{"disambiguationData":[OSD([sQuery(id+"F24.wireOp",EDGE,"E127")])]})])],"derivedFrom":makeQuery(id+"F23.boolean.opBoolean","COPY",EDGE,{"derivedFrom":makeQuery(id+"F23.opExtrude","CAP_EDGE",EDGE,{"disambiguationData":[OSD([subQ0])],"isStart":true})})})});}
            var Q20;
            Q20=makeQuery(id+"F26.opPattern","COPY",EDGE,{"derivedFrom":makeQuery(id+"F25.boolean.opBoolean","INTERSECT",EDGE,{"disambiguationData":[OD(0.0)],"derivedFrom":[makeQuery(id+"F23.boolean.opBoolean","COPY",FACE,{"derivedFrom":makeQuery(id+"F23.opExtrude","SWEPT_FACE",FACE,{"disambiguationData":[OSD([sQuery(id+"F22.wireOp",EDGE,"E123")])]})}),makeQuery(id+"F25.opExtrude","SWEPT_FACE",FACE,{"disambiguationData":[OSD([sQuery(id+"F24.wireOp",EDGE,"E127")])]})]}),"instanceName":"2"});
            var Q21;
            Q21=makeQuery(id+"F26.opPattern","COPY",EDGE,{"derivedFrom":makeQuery(id+"F25.boolean.opBoolean","INTERSECT",EDGE,{"disambiguationData":[OD(0.0)],"derivedFrom":[makeQuery(id+"F23.boolean.opBoolean","COPY",FACE,{"derivedFrom":makeQuery(id+"F23.opExtrude","SWEPT_FACE",FACE,{"disambiguationData":[OSD([sQuery(id+"F22.wireOp",EDGE,"E123")])]})}),makeQuery(id+"F25.opExtrude","SWEPT_FACE",FACE,{"disambiguationData":[OSD([sQuery(id+"F24.wireOp",EDGE,"E126")])]})]}),"instanceName":"2"});
            var Q22;
            {var subQ0=sQuery(id+"F22.wireOp",EDGE,"E123");Q22=makeQuery(id+"F26.opPattern","SPLIT",EDGE,{"disambiguationData":[OD(2.0)],"derivedFrom":makeQuery(id+"F25.boolean.opBoolean","SPLIT",EDGE,{"disambiguationData":[TD([makeQuery(id+"F25.opExtrude","SWEPT_FACE",FACE,{"disambiguationData":[OSD([sQuery(id+"F24.wireOp",EDGE,"E127")])]})])],"derivedFrom":makeQuery(id+"F23.boolean.opBoolean","COPY",EDGE,{"derivedFrom":makeQuery(id+"F23.opExtrude","CAP_EDGE",EDGE,{"disambiguationData":[OSD([subQ0])],"isStart":true})})})});}
            var Q23;
            Q23=makeQuery(id+"F26.opPattern","COPY",EDGE,{"derivedFrom":makeQuery(id+"F25.boolean.opBoolean","INTERSECT",EDGE,{"disambiguationData":[OD(0.0)],"derivedFrom":[makeQuery(id+"F23.boolean.opBoolean","COPY",FACE,{"derivedFrom":makeQuery(id+"F23.opExtrude","SWEPT_FACE",FACE,{"disambiguationData":[OSD([sQuery(id+"F22.wireOp",EDGE,"E123")])]})}),makeQuery(id+"F25.opExtrude","SWEPT_FACE",FACE,{"disambiguationData":[OSD([sQuery(id+"F24.wireOp",EDGE,"E127")])]})]}),"instanceName":"1"});
            var Q24;
            Q24=makeQuery(id+"F26.opPattern","COPY",EDGE,{"derivedFrom":makeQuery(id+"F25.boolean.opBoolean","INTERSECT",EDGE,{"disambiguationData":[OD(0.0)],"derivedFrom":[makeQuery(id+"F23.boolean.opBoolean","COPY",FACE,{"derivedFrom":makeQuery(id+"F23.opExtrude","SWEPT_FACE",FACE,{"disambiguationData":[OSD([sQuery(id+"F22.wireOp",EDGE,"E123")])]})}),makeQuery(id+"F25.opExtrude","SWEPT_FACE",FACE,{"disambiguationData":[OSD([sQuery(id+"F24.wireOp",EDGE,"E126")])]})]}),"instanceName":"1"});
            var Q25;
            {var subQ0=sQuery(id+"F22.wireOp",EDGE,"E123");Q25=makeQuery(id+"F26.opPattern","SPLIT",EDGE,{"disambiguationData":[OD(0.0)],"derivedFrom":makeQuery(id+"F25.boolean.opBoolean","SPLIT",EDGE,{"disambiguationData":[TD([makeQuery(id+"F25.opExtrude","SWEPT_FACE",FACE,{"disambiguationData":[OSD([sQuery(id+"F24.wireOp",EDGE,"E127")])]})])],"derivedFrom":makeQuery(id+"F23.boolean.opBoolean","COPY",EDGE,{"derivedFrom":makeQuery(id+"F23.opExtrude","CAP_EDGE",EDGE,{"disambiguationData":[OSD([subQ0])],"isStart":true})})})});}
            var Q26;
            Q26=makeQuery(id+"F25.boolean.opBoolean","INTERSECT",EDGE,{"disambiguationData":[OD(0.0)],"derivedFrom":[makeQuery(id+"F23.boolean.opBoolean","COPY",FACE,{"derivedFrom":makeQuery(id+"F23.opExtrude","SWEPT_FACE",FACE,{"disambiguationData":[OSD([sQuery(id+"F22.wireOp",EDGE,"E123")])]})}),makeQuery(id+"F25.opExtrude","SWEPT_FACE",FACE,{"disambiguationData":[OSD([sQuery(id+"F24.wireOp",EDGE,"E127")])]})]});
            var Q27;
            Q27=makeQuery(id+"F25.boolean.opBoolean","INTERSECT",EDGE,{"disambiguationData":[OD(0.0)],"derivedFrom":[makeQuery(id+"F23.boolean.opBoolean","COPY",FACE,{"derivedFrom":makeQuery(id+"F23.opExtrude","SWEPT_FACE",FACE,{"disambiguationData":[OSD([sQuery(id+"F22.wireOp",EDGE,"E123")])]})}),makeQuery(id+"F25.opExtrude","SWEPT_FACE",FACE,{"disambiguationData":[OSD([sQuery(id+"F24.wireOp",EDGE,"E126")])]})]});
            var Q28;
            {var subQ0=sQuery(id+"F22.wireOp",EDGE,"E123");Q28=makeQuery(id+"F26.opPattern","SPLIT",EDGE,{"disambiguationData":[OD(0.0)],"derivedFrom":makeQuery(id+"F25.boolean.opBoolean","SPLIT",EDGE,{"disambiguationData":[TD([makeQuery(id+"F25.opExtrude","SWEPT_FACE",FACE,{"disambiguationData":[OSD([sQuery(id+"F24.wireOp",EDGE,"E126")])]})])],"derivedFrom":makeQuery(id+"F23.boolean.opBoolean","COPY",EDGE,{"derivedFrom":makeQuery(id+"F23.opExtrude","CAP_EDGE",EDGE,{"disambiguationData":[OSD([subQ0])],"isStart":true})})})});}
            var Q29;
            Q29=makeQuery(id+"F26.opPattern","COPY",EDGE,{"derivedFrom":makeQuery(id+"F25.boolean.opBoolean","INTERSECT",EDGE,{"disambiguationData":[OD(1.0)],"derivedFrom":[makeQuery(id+"F23.boolean.opBoolean","COPY",FACE,{"derivedFrom":makeQuery(id+"F23.opExtrude","SWEPT_FACE",FACE,{"disambiguationData":[OSD([sQuery(id+"F22.wireOp",EDGE,"E123")])]})}),makeQuery(id+"F25.opExtrude","SWEPT_FACE",FACE,{"disambiguationData":[OSD([sQuery(id+"F24.wireOp",EDGE,"E126")])]})]}),"instanceName":"7"});
            var Q30;
            Q30=makeQuery(id+"F26.opPattern","COPY",EDGE,{"derivedFrom":makeQuery(id+"F25.boolean.opBoolean","INTERSECT",EDGE,{"disambiguationData":[OD(1.0)],"derivedFrom":[makeQuery(id+"F23.boolean.opBoolean","COPY",FACE,{"derivedFrom":makeQuery(id+"F23.opExtrude","SWEPT_FACE",FACE,{"disambiguationData":[OSD([sQuery(id+"F22.wireOp",EDGE,"E123")])]})}),makeQuery(id+"F25.opExtrude","SWEPT_FACE",FACE,{"disambiguationData":[OSD([sQuery(id+"F24.wireOp",EDGE,"E127")])]})]}),"instanceName":"7"});
            var Q31;
            {var subQ0=sQuery(id+"F22.wireOp",EDGE,"E123");Q31=makeQuery(id+"F26.opPattern","SPLIT",EDGE,{"disambiguationData":[OD(7.0)],"derivedFrom":makeQuery(id+"F25.boolean.opBoolean","SPLIT",EDGE,{"disambiguationData":[TD([makeQuery(id+"F25.opExtrude","SWEPT_FACE",FACE,{"disambiguationData":[OSD([sQuery(id+"F24.wireOp",EDGE,"E126")])]})])],"derivedFrom":makeQuery(id+"F23.boolean.opBoolean","COPY",EDGE,{"derivedFrom":makeQuery(id+"F23.opExtrude","CAP_EDGE",EDGE,{"disambiguationData":[OSD([subQ0])],"isStart":true})})})});}
            var Q32;
            Q32=makeQuery(id+"F26.opPattern","COPY",EDGE,{"derivedFrom":makeQuery(id+"F25.boolean.opBoolean","INTERSECT",EDGE,{"disambiguationData":[OD(1.0)],"derivedFrom":[makeQuery(id+"F23.boolean.opBoolean","COPY",FACE,{"derivedFrom":makeQuery(id+"F23.opExtrude","SWEPT_FACE",FACE,{"disambiguationData":[OSD([sQuery(id+"F22.wireOp",EDGE,"E123")])]})}),makeQuery(id+"F25.opExtrude","SWEPT_FACE",FACE,{"disambiguationData":[OSD([sQuery(id+"F24.wireOp",EDGE,"E126")])]})]}),"instanceName":"6"});
            var Q33;
            Q33=makeQuery(id+"F26.opPattern","COPY",EDGE,{"derivedFrom":makeQuery(id+"F25.boolean.opBoolean","INTERSECT",EDGE,{"disambiguationData":[OD(1.0)],"derivedFrom":[makeQuery(id+"F23.boolean.opBoolean","COPY",FACE,{"derivedFrom":makeQuery(id+"F23.opExtrude","SWEPT_FACE",FACE,{"disambiguationData":[OSD([sQuery(id+"F22.wireOp",EDGE,"E123")])]})}),makeQuery(id+"F25.opExtrude","SWEPT_FACE",FACE,{"disambiguationData":[OSD([sQuery(id+"F24.wireOp",EDGE,"E127")])]})]}),"instanceName":"6"});
            var Q34;
            {var subQ0=sQuery(id+"F22.wireOp",EDGE,"E123");Q34=makeQuery(id+"F26.opPattern","SPLIT",EDGE,{"disambiguationData":[OD(6.0)],"derivedFrom":makeQuery(id+"F25.boolean.opBoolean","SPLIT",EDGE,{"disambiguationData":[TD([makeQuery(id+"F25.opExtrude","SWEPT_FACE",FACE,{"disambiguationData":[OSD([sQuery(id+"F24.wireOp",EDGE,"E126")])]})])],"derivedFrom":makeQuery(id+"F23.boolean.opBoolean","COPY",EDGE,{"derivedFrom":makeQuery(id+"F23.opExtrude","CAP_EDGE",EDGE,{"disambiguationData":[OSD([subQ0])],"isStart":true})})})});}
            var Q35;
            Q35=makeQuery(id+"F26.opPattern","COPY",EDGE,{"derivedFrom":makeQuery(id+"F25.boolean.opBoolean","INTERSECT",EDGE,{"disambiguationData":[OD(1.0)],"derivedFrom":[makeQuery(id+"F23.boolean.opBoolean","COPY",FACE,{"derivedFrom":makeQuery(id+"F23.opExtrude","SWEPT_FACE",FACE,{"disambiguationData":[OSD([sQuery(id+"F22.wireOp",EDGE,"E123")])]})}),makeQuery(id+"F25.opExtrude","SWEPT_FACE",FACE,{"disambiguationData":[OSD([sQuery(id+"F24.wireOp",EDGE,"E126")])]})]}),"instanceName":"5"});
            var Q36;
            Q36=makeQuery(id+"F26.opPattern","COPY",EDGE,{"derivedFrom":makeQuery(id+"F25.boolean.opBoolean","INTERSECT",EDGE,{"disambiguationData":[OD(1.0)],"derivedFrom":[makeQuery(id+"F23.boolean.opBoolean","COPY",FACE,{"derivedFrom":makeQuery(id+"F23.opExtrude","SWEPT_FACE",FACE,{"disambiguationData":[OSD([sQuery(id+"F22.wireOp",EDGE,"E123")])]})}),makeQuery(id+"F25.opExtrude","SWEPT_FACE",FACE,{"disambiguationData":[OSD([sQuery(id+"F24.wireOp",EDGE,"E127")])]})]}),"instanceName":"5"});
            var Q37;
            {var subQ0=sQuery(id+"F22.wireOp",EDGE,"E123");Q37=makeQuery(id+"F26.opPattern","SPLIT",EDGE,{"disambiguationData":[OD(5.0)],"derivedFrom":makeQuery(id+"F25.boolean.opBoolean","SPLIT",EDGE,{"disambiguationData":[TD([makeQuery(id+"F25.opExtrude","SWEPT_FACE",FACE,{"disambiguationData":[OSD([sQuery(id+"F24.wireOp",EDGE,"E126")])]})])],"derivedFrom":makeQuery(id+"F23.boolean.opBoolean","COPY",EDGE,{"derivedFrom":makeQuery(id+"F23.opExtrude","CAP_EDGE",EDGE,{"disambiguationData":[OSD([subQ0])],"isStart":true})})})});}
            var Q38;
            Q38=makeQuery(id+"F26.opPattern","COPY",EDGE,{"derivedFrom":makeQuery(id+"F25.boolean.opBoolean","INTERSECT",EDGE,{"disambiguationData":[OD(1.0)],"derivedFrom":[makeQuery(id+"F23.boolean.opBoolean","COPY",FACE,{"derivedFrom":makeQuery(id+"F23.opExtrude","SWEPT_FACE",FACE,{"disambiguationData":[OSD([sQuery(id+"F22.wireOp",EDGE,"E123")])]})}),makeQuery(id+"F25.opExtrude","SWEPT_FACE",FACE,{"disambiguationData":[OSD([sQuery(id+"F24.wireOp",EDGE,"E126")])]})]}),"instanceName":"4"});
            var Q39;
            Q39=makeQuery(id+"F26.opPattern","COPY",EDGE,{"derivedFrom":makeQuery(id+"F25.boolean.opBoolean","INTERSECT",EDGE,{"disambiguationData":[OD(1.0)],"derivedFrom":[makeQuery(id+"F23.boolean.opBoolean","COPY",FACE,{"derivedFrom":makeQuery(id+"F23.opExtrude","SWEPT_FACE",FACE,{"disambiguationData":[OSD([sQuery(id+"F22.wireOp",EDGE,"E123")])]})}),makeQuery(id+"F25.opExtrude","SWEPT_FACE",FACE,{"disambiguationData":[OSD([sQuery(id+"F24.wireOp",EDGE,"E127")])]})]}),"instanceName":"4"});
            var Q40;
            {var subQ0=sQuery(id+"F22.wireOp",EDGE,"E123");Q40=makeQuery(id+"F26.opPattern","SPLIT",EDGE,{"disambiguationData":[OD(4.0)],"derivedFrom":makeQuery(id+"F25.boolean.opBoolean","SPLIT",EDGE,{"disambiguationData":[TD([makeQuery(id+"F25.opExtrude","SWEPT_FACE",FACE,{"disambiguationData":[OSD([sQuery(id+"F24.wireOp",EDGE,"E126")])]})])],"derivedFrom":makeQuery(id+"F23.boolean.opBoolean","COPY",EDGE,{"derivedFrom":makeQuery(id+"F23.opExtrude","CAP_EDGE",EDGE,{"disambiguationData":[OSD([subQ0])],"isStart":true})})})});}
            var Q41;
            Q41=makeQuery(id+"F26.opPattern","COPY",EDGE,{"derivedFrom":makeQuery(id+"F25.boolean.opBoolean","INTERSECT",EDGE,{"disambiguationData":[OD(1.0)],"derivedFrom":[makeQuery(id+"F23.boolean.opBoolean","COPY",FACE,{"derivedFrom":makeQuery(id+"F23.opExtrude","SWEPT_FACE",FACE,{"disambiguationData":[OSD([sQuery(id+"F22.wireOp",EDGE,"E123")])]})}),makeQuery(id+"F25.opExtrude","SWEPT_FACE",FACE,{"disambiguationData":[OSD([sQuery(id+"F24.wireOp",EDGE,"E126")])]})]}),"instanceName":"3"});
            var Q42;
            Q42=makeQuery(id+"F26.opPattern","COPY",EDGE,{"derivedFrom":makeQuery(id+"F25.boolean.opBoolean","INTERSECT",EDGE,{"disambiguationData":[OD(1.0)],"derivedFrom":[makeQuery(id+"F23.boolean.opBoolean","COPY",FACE,{"derivedFrom":makeQuery(id+"F23.opExtrude","SWEPT_FACE",FACE,{"disambiguationData":[OSD([sQuery(id+"F22.wireOp",EDGE,"E123")])]})}),makeQuery(id+"F25.opExtrude","SWEPT_FACE",FACE,{"disambiguationData":[OSD([sQuery(id+"F24.wireOp",EDGE,"E127")])]})]}),"instanceName":"3"});
            var Q43;
            {var subQ0=sQuery(id+"F22.wireOp",EDGE,"E123");Q43=makeQuery(id+"F26.opPattern","SPLIT",EDGE,{"disambiguationData":[OD(3.0)],"derivedFrom":makeQuery(id+"F25.boolean.opBoolean","SPLIT",EDGE,{"disambiguationData":[TD([makeQuery(id+"F25.opExtrude","SWEPT_FACE",FACE,{"disambiguationData":[OSD([sQuery(id+"F24.wireOp",EDGE,"E126")])]})])],"derivedFrom":makeQuery(id+"F23.boolean.opBoolean","COPY",EDGE,{"derivedFrom":makeQuery(id+"F23.opExtrude","CAP_EDGE",EDGE,{"disambiguationData":[OSD([subQ0])],"isStart":true})})})});}
            var Q44;
            Q44=makeQuery(id+"F26.opPattern","COPY",EDGE,{"derivedFrom":makeQuery(id+"F25.boolean.opBoolean","INTERSECT",EDGE,{"disambiguationData":[OD(1.0)],"derivedFrom":[makeQuery(id+"F23.boolean.opBoolean","COPY",FACE,{"derivedFrom":makeQuery(id+"F23.opExtrude","SWEPT_FACE",FACE,{"disambiguationData":[OSD([sQuery(id+"F22.wireOp",EDGE,"E123")])]})}),makeQuery(id+"F25.opExtrude","SWEPT_FACE",FACE,{"disambiguationData":[OSD([sQuery(id+"F24.wireOp",EDGE,"E126")])]})]}),"instanceName":"2"});
            var Q45;
            Q45=makeQuery(id+"F26.opPattern","COPY",EDGE,{"derivedFrom":makeQuery(id+"F25.boolean.opBoolean","INTERSECT",EDGE,{"disambiguationData":[OD(1.0)],"derivedFrom":[makeQuery(id+"F23.boolean.opBoolean","COPY",FACE,{"derivedFrom":makeQuery(id+"F23.opExtrude","SWEPT_FACE",FACE,{"disambiguationData":[OSD([sQuery(id+"F22.wireOp",EDGE,"E123")])]})}),makeQuery(id+"F25.opExtrude","SWEPT_FACE",FACE,{"disambiguationData":[OSD([sQuery(id+"F24.wireOp",EDGE,"E127")])]})]}),"instanceName":"2"});
            var Q46;
            {var subQ0=sQuery(id+"F22.wireOp",EDGE,"E123");Q46=makeQuery(id+"F26.opPattern","SPLIT",EDGE,{"disambiguationData":[OD(2.0)],"derivedFrom":makeQuery(id+"F25.boolean.opBoolean","SPLIT",EDGE,{"disambiguationData":[TD([makeQuery(id+"F25.opExtrude","SWEPT_FACE",FACE,{"disambiguationData":[OSD([sQuery(id+"F24.wireOp",EDGE,"E126")])]})])],"derivedFrom":makeQuery(id+"F23.boolean.opBoolean","COPY",EDGE,{"derivedFrom":makeQuery(id+"F23.opExtrude","CAP_EDGE",EDGE,{"disambiguationData":[OSD([subQ0])],"isStart":true})})})});}
            var Q47;
            Q47=makeQuery(id+"F26.opPattern","COPY",EDGE,{"derivedFrom":makeQuery(id+"F25.boolean.opBoolean","INTERSECT",EDGE,{"disambiguationData":[OD(1.0)],"derivedFrom":[makeQuery(id+"F23.boolean.opBoolean","COPY",FACE,{"derivedFrom":makeQuery(id+"F23.opExtrude","SWEPT_FACE",FACE,{"disambiguationData":[OSD([sQuery(id+"F22.wireOp",EDGE,"E123")])]})}),makeQuery(id+"F25.opExtrude","SWEPT_FACE",FACE,{"disambiguationData":[OSD([sQuery(id+"F24.wireOp",EDGE,"E126")])]})]}),"instanceName":"1"});
            fillet(context, id + "F27", {"entities" : qUnion([Q0, Q1, Q2, Q3, Q4, Q5, Q6, Q7, Q8, Q9, Q10, Q11, Q12, Q13, Q14, Q15, Q16, Q17, Q18, Q19, Q20, Q21, Q22, Q23, Q24, Q25, Q26, Q27, Q28, Q29, Q30, Q31, Q32, Q33, Q34, Q35, Q36, Q37, Q38, Q39, Q40, Q41, Q42, Q43, Q44, Q45, Q46, Q47]), "radius" : 0.5 * mm, "tangentPropagation" : true, "allowEdgeOverflow" : false});
        }
        {
            var Q0;
            {var subQ0=sQuery(id+"F14.wireOp",EDGE,"E74");var subQ1=sQuery(id+"F14.wireOp",EDGE,"E75");Q0=makeQuery(id+"F26.opPattern","SPLIT",EDGE,{"disambiguationData":[OD(3.0)],"derivedFrom":makeQuery(id+"F25.boolean.opBoolean","SPLIT",EDGE,{"disambiguationData":[TD([makeQuery(id+"F25.opExtrude","SWEPT_FACE",FACE,{"disambiguationData":[OSD([sQuery(id+"F24.wireOp",EDGE,"E127")])]})])],"derivedFrom":makeQuery(id+"F15.opRevolve","SWEPT_EDGE",EDGE,{"disambiguationData":[OSD([subQ0,subQ1])]})})});}
            var Q1;
            Q1=makeQuery(id+"F26.opPattern","COPY",EDGE,{"derivedFrom":makeQuery(id+"F25.boolean.opBoolean","INTERSECT",EDGE,{"disambiguationData":[OD(0.0)],"derivedFrom":[makeQuery(id+"F15.opRevolve","SWEPT_FACE",FACE,{"disambiguationData":[OSD([sQuery(id+"F14.wireOp",EDGE,"E75")])]}),makeQuery(id+"F25.opExtrude","SWEPT_FACE",FACE,{"disambiguationData":[OSD([sQuery(id+"F24.wireOp",EDGE,"E127")])]})]}),"instanceName":"2"});
            var Q2;
            Q2=makeQuery(id+"F26.opPattern","COPY",EDGE,{"derivedFrom":makeQuery(id+"F25.boolean.opBoolean","INTERSECT",EDGE,{"disambiguationData":[OD(0.0)],"derivedFrom":[makeQuery(id+"F15.opRevolve","SWEPT_FACE",FACE,{"disambiguationData":[OSD([sQuery(id+"F14.wireOp",EDGE,"E75")])]}),makeQuery(id+"F25.opExtrude","SWEPT_FACE",FACE,{"disambiguationData":[OSD([sQuery(id+"F24.wireOp",EDGE,"E126")])]})]}),"instanceName":"2"});
            var Q3;
            {var subQ0=sQuery(id+"F14.wireOp",EDGE,"E74");var subQ1=sQuery(id+"F14.wireOp",EDGE,"E75");Q3=makeQuery(id+"F26.opPattern","SPLIT",EDGE,{"disambiguationData":[OD(2.0)],"derivedFrom":makeQuery(id+"F25.boolean.opBoolean","SPLIT",EDGE,{"disambiguationData":[TD([makeQuery(id+"F25.opExtrude","SWEPT_FACE",FACE,{"disambiguationData":[OSD([sQuery(id+"F24.wireOp",EDGE,"E127")])]})])],"derivedFrom":makeQuery(id+"F15.opRevolve","SWEPT_EDGE",EDGE,{"disambiguationData":[OSD([subQ0,subQ1])]})})});}
            var Q4;
            Q4=makeQuery(id+"F26.opPattern","COPY",EDGE,{"derivedFrom":makeQuery(id+"F25.boolean.opBoolean","INTERSECT",EDGE,{"disambiguationData":[OD(0.0)],"derivedFrom":[makeQuery(id+"F15.opRevolve","SWEPT_FACE",FACE,{"disambiguationData":[OSD([sQuery(id+"F14.wireOp",EDGE,"E75")])]}),makeQuery(id+"F25.opExtrude","SWEPT_FACE",FACE,{"disambiguationData":[OSD([sQuery(id+"F24.wireOp",EDGE,"E127")])]})]}),"instanceName":"1"});
            var Q5;
            Q5=makeQuery(id+"F26.opPattern","COPY",EDGE,{"derivedFrom":makeQuery(id+"F25.boolean.opBoolean","INTERSECT",EDGE,{"disambiguationData":[OD(0.0)],"derivedFrom":[makeQuery(id+"F15.opRevolve","SWEPT_FACE",FACE,{"disambiguationData":[OSD([sQuery(id+"F14.wireOp",EDGE,"E75")])]}),makeQuery(id+"F25.opExtrude","SWEPT_FACE",FACE,{"disambiguationData":[OSD([sQuery(id+"F24.wireOp",EDGE,"E126")])]})]}),"instanceName":"1"});
            var Q6;
            {var subQ0=sQuery(id+"F14.wireOp",EDGE,"E74");var subQ1=sQuery(id+"F14.wireOp",EDGE,"E75");Q6=makeQuery(id+"F26.opPattern","SPLIT",EDGE,{"disambiguationData":[OD(0.0)],"derivedFrom":makeQuery(id+"F25.boolean.opBoolean","SPLIT",EDGE,{"disambiguationData":[TD([makeQuery(id+"F25.opExtrude","SWEPT_FACE",FACE,{"disambiguationData":[OSD([sQuery(id+"F24.wireOp",EDGE,"E127")])]})])],"derivedFrom":makeQuery(id+"F15.opRevolve","SWEPT_EDGE",EDGE,{"disambiguationData":[OSD([subQ0,subQ1])]})})});}
            var Q7;
            Q7=makeQuery(id+"F25.boolean.opBoolean","INTERSECT",EDGE,{"disambiguationData":[OD(0.0)],"derivedFrom":[makeQuery(id+"F15.opRevolve","SWEPT_FACE",FACE,{"disambiguationData":[OSD([sQuery(id+"F14.wireOp",EDGE,"E75")])]}),makeQuery(id+"F25.opExtrude","SWEPT_FACE",FACE,{"disambiguationData":[OSD([sQuery(id+"F24.wireOp",EDGE,"E127")])]})]});
            var Q8;
            Q8=makeQuery(id+"F25.boolean.opBoolean","INTERSECT",EDGE,{"disambiguationData":[OD(0.0)],"derivedFrom":[makeQuery(id+"F15.opRevolve","SWEPT_FACE",FACE,{"disambiguationData":[OSD([sQuery(id+"F14.wireOp",EDGE,"E75")])]}),makeQuery(id+"F25.opExtrude","SWEPT_FACE",FACE,{"disambiguationData":[OSD([sQuery(id+"F24.wireOp",EDGE,"E126")])]})]});
            var Q9;
            {var subQ0=sQuery(id+"F14.wireOp",EDGE,"E74");var subQ1=sQuery(id+"F14.wireOp",EDGE,"E75");Q9=makeQuery(id+"F26.opPattern","SPLIT",EDGE,{"disambiguationData":[OD(0.0)],"derivedFrom":makeQuery(id+"F25.boolean.opBoolean","SPLIT",EDGE,{"disambiguationData":[TD([makeQuery(id+"F25.opExtrude","SWEPT_FACE",FACE,{"disambiguationData":[OSD([sQuery(id+"F24.wireOp",EDGE,"E126")])]})])],"derivedFrom":makeQuery(id+"F15.opRevolve","SWEPT_EDGE",EDGE,{"disambiguationData":[OSD([subQ0,subQ1])]})})});}
            var Q10;
            Q10=makeQuery(id+"F26.opPattern","COPY",EDGE,{"derivedFrom":makeQuery(id+"F25.boolean.opBoolean","INTERSECT",EDGE,{"disambiguationData":[OD(1.0)],"derivedFrom":[makeQuery(id+"F15.opRevolve","SWEPT_FACE",FACE,{"disambiguationData":[OSD([sQuery(id+"F14.wireOp",EDGE,"E75")])]}),makeQuery(id+"F25.opExtrude","SWEPT_FACE",FACE,{"disambiguationData":[OSD([sQuery(id+"F24.wireOp",EDGE,"E126")])]})]}),"instanceName":"7"});
            var Q11;
            Q11=makeQuery(id+"F26.opPattern","COPY",EDGE,{"derivedFrom":makeQuery(id+"F25.boolean.opBoolean","INTERSECT",EDGE,{"disambiguationData":[OD(1.0)],"derivedFrom":[makeQuery(id+"F15.opRevolve","SWEPT_FACE",FACE,{"disambiguationData":[OSD([sQuery(id+"F14.wireOp",EDGE,"E75")])]}),makeQuery(id+"F25.opExtrude","SWEPT_FACE",FACE,{"disambiguationData":[OSD([sQuery(id+"F24.wireOp",EDGE,"E127")])]})]}),"instanceName":"7"});
            var Q12;
            {var subQ0=sQuery(id+"F14.wireOp",EDGE,"E74");var subQ1=sQuery(id+"F14.wireOp",EDGE,"E75");Q12=makeQuery(id+"F26.opPattern","SPLIT",EDGE,{"disambiguationData":[OD(7.0)],"derivedFrom":makeQuery(id+"F25.boolean.opBoolean","SPLIT",EDGE,{"disambiguationData":[TD([makeQuery(id+"F25.opExtrude","SWEPT_FACE",FACE,{"disambiguationData":[OSD([sQuery(id+"F24.wireOp",EDGE,"E126")])]})])],"derivedFrom":makeQuery(id+"F15.opRevolve","SWEPT_EDGE",EDGE,{"disambiguationData":[OSD([subQ0,subQ1])]})})});}
            var Q13;
            Q13=makeQuery(id+"F26.opPattern","COPY",EDGE,{"derivedFrom":makeQuery(id+"F25.boolean.opBoolean","INTERSECT",EDGE,{"disambiguationData":[OD(1.0)],"derivedFrom":[makeQuery(id+"F15.opRevolve","SWEPT_FACE",FACE,{"disambiguationData":[OSD([sQuery(id+"F14.wireOp",EDGE,"E75")])]}),makeQuery(id+"F25.opExtrude","SWEPT_FACE",FACE,{"disambiguationData":[OSD([sQuery(id+"F24.wireOp",EDGE,"E126")])]})]}),"instanceName":"6"});
            var Q14;
            Q14=makeQuery(id+"F26.opPattern","COPY",EDGE,{"derivedFrom":makeQuery(id+"F25.boolean.opBoolean","INTERSECT",EDGE,{"disambiguationData":[OD(1.0)],"derivedFrom":[makeQuery(id+"F15.opRevolve","SWEPT_FACE",FACE,{"disambiguationData":[OSD([sQuery(id+"F14.wireOp",EDGE,"E75")])]}),makeQuery(id+"F25.opExtrude","SWEPT_FACE",FACE,{"disambiguationData":[OSD([sQuery(id+"F24.wireOp",EDGE,"E127")])]})]}),"instanceName":"6"});
            var Q15;
            {var subQ0=sQuery(id+"F14.wireOp",EDGE,"E74");var subQ1=sQuery(id+"F14.wireOp",EDGE,"E75");Q15=makeQuery(id+"F26.opPattern","SPLIT",EDGE,{"disambiguationData":[OD(6.0)],"derivedFrom":makeQuery(id+"F25.boolean.opBoolean","SPLIT",EDGE,{"disambiguationData":[TD([makeQuery(id+"F25.opExtrude","SWEPT_FACE",FACE,{"disambiguationData":[OSD([sQuery(id+"F24.wireOp",EDGE,"E126")])]})])],"derivedFrom":makeQuery(id+"F15.opRevolve","SWEPT_EDGE",EDGE,{"disambiguationData":[OSD([subQ0,subQ1])]})})});}
            var Q16;
            Q16=makeQuery(id+"F26.opPattern","COPY",EDGE,{"derivedFrom":makeQuery(id+"F25.boolean.opBoolean","INTERSECT",EDGE,{"disambiguationData":[OD(1.0)],"derivedFrom":[makeQuery(id+"F15.opRevolve","SWEPT_FACE",FACE,{"disambiguationData":[OSD([sQuery(id+"F14.wireOp",EDGE,"E75")])]}),makeQuery(id+"F25.opExtrude","SWEPT_FACE",FACE,{"disambiguationData":[OSD([sQuery(id+"F24.wireOp",EDGE,"E126")])]})]}),"instanceName":"5"});
            var Q17;
            Q17=makeQuery(id+"F26.opPattern","COPY",EDGE,{"derivedFrom":makeQuery(id+"F25.boolean.opBoolean","INTERSECT",EDGE,{"disambiguationData":[OD(1.0)],"derivedFrom":[makeQuery(id+"F15.opRevolve","SWEPT_FACE",FACE,{"disambiguationData":[OSD([sQuery(id+"F14.wireOp",EDGE,"E75")])]}),makeQuery(id+"F25.opExtrude","SWEPT_FACE",FACE,{"disambiguationData":[OSD([sQuery(id+"F24.wireOp",EDGE,"E127")])]})]}),"instanceName":"5"});
            var Q18;
            {var subQ0=sQuery(id+"F14.wireOp",EDGE,"E74");var subQ1=sQuery(id+"F14.wireOp",EDGE,"E75");Q18=makeQuery(id+"F26.opPattern","SPLIT",EDGE,{"disambiguationData":[OD(5.0)],"derivedFrom":makeQuery(id+"F25.boolean.opBoolean","SPLIT",EDGE,{"disambiguationData":[TD([makeQuery(id+"F25.opExtrude","SWEPT_FACE",FACE,{"disambiguationData":[OSD([sQuery(id+"F24.wireOp",EDGE,"E126")])]})])],"derivedFrom":makeQuery(id+"F15.opRevolve","SWEPT_EDGE",EDGE,{"disambiguationData":[OSD([subQ0,subQ1])]})})});}
            var Q19;
            Q19=makeQuery(id+"F26.opPattern","COPY",EDGE,{"derivedFrom":makeQuery(id+"F25.boolean.opBoolean","INTERSECT",EDGE,{"disambiguationData":[OD(1.0)],"derivedFrom":[makeQuery(id+"F15.opRevolve","SWEPT_FACE",FACE,{"disambiguationData":[OSD([sQuery(id+"F14.wireOp",EDGE,"E75")])]}),makeQuery(id+"F25.opExtrude","SWEPT_FACE",FACE,{"disambiguationData":[OSD([sQuery(id+"F24.wireOp",EDGE,"E126")])]})]}),"instanceName":"4"});
            var Q20;
            Q20=makeQuery(id+"F26.opPattern","COPY",EDGE,{"derivedFrom":makeQuery(id+"F25.boolean.opBoolean","INTERSECT",EDGE,{"disambiguationData":[OD(1.0)],"derivedFrom":[makeQuery(id+"F15.opRevolve","SWEPT_FACE",FACE,{"disambiguationData":[OSD([sQuery(id+"F14.wireOp",EDGE,"E75")])]}),makeQuery(id+"F25.opExtrude","SWEPT_FACE",FACE,{"disambiguationData":[OSD([sQuery(id+"F24.wireOp",EDGE,"E127")])]})]}),"instanceName":"4"});
            var Q21;
            Q21=makeQuery(id+"F26.opPattern","COPY",EDGE,{"derivedFrom":makeQuery(id+"F25.boolean.opBoolean","INTERSECT",EDGE,{"disambiguationData":[OD(0.0)],"derivedFrom":[makeQuery(id+"F15.opRevolve","SWEPT_FACE",FACE,{"disambiguationData":[OSD([sQuery(id+"F14.wireOp",EDGE,"E75")])]}),makeQuery(id+"F25.opExtrude","SWEPT_FACE",FACE,{"disambiguationData":[OSD([sQuery(id+"F24.wireOp",EDGE,"E126")])]})]}),"instanceName":"3"});
            var Q22;
            Q22=makeQuery(id+"F26.opPattern","COPY",EDGE,{"derivedFrom":makeQuery(id+"F25.boolean.opBoolean","INTERSECT",EDGE,{"disambiguationData":[OD(0.0)],"derivedFrom":[makeQuery(id+"F15.opRevolve","SWEPT_FACE",FACE,{"disambiguationData":[OSD([sQuery(id+"F14.wireOp",EDGE,"E75")])]}),makeQuery(id+"F25.opExtrude","SWEPT_FACE",FACE,{"disambiguationData":[OSD([sQuery(id+"F24.wireOp",EDGE,"E127")])]})]}),"instanceName":"3"});
            var Q23;
            {var subQ0=sQuery(id+"F14.wireOp",EDGE,"E74");var subQ1=sQuery(id+"F14.wireOp",EDGE,"E75");Q23=makeQuery(id+"F26.opPattern","SPLIT",EDGE,{"disambiguationData":[OD(4.0)],"derivedFrom":makeQuery(id+"F25.boolean.opBoolean","SPLIT",EDGE,{"disambiguationData":[TD([makeQuery(id+"F25.opExtrude","SWEPT_FACE",FACE,{"disambiguationData":[OSD([sQuery(id+"F24.wireOp",EDGE,"E127")])]})])],"derivedFrom":makeQuery(id+"F15.opRevolve","SWEPT_EDGE",EDGE,{"disambiguationData":[OSD([subQ0,subQ1])]})})});}
            var Q24;
            Q24=makeQuery(id+"F26.opPattern","COPY",EDGE,{"derivedFrom":makeQuery(id+"F25.boolean.opBoolean","INTERSECT",EDGE,{"disambiguationData":[OD(0.0)],"derivedFrom":[makeQuery(id+"F15.opRevolve","SWEPT_FACE",FACE,{"disambiguationData":[OSD([sQuery(id+"F14.wireOp",EDGE,"E75")])]}),makeQuery(id+"F25.opExtrude","SWEPT_FACE",FACE,{"disambiguationData":[OSD([sQuery(id+"F24.wireOp",EDGE,"E126")])]})]}),"instanceName":"4"});
            var Q25;
            Q25=makeQuery(id+"F26.opPattern","COPY",EDGE,{"derivedFrom":makeQuery(id+"F25.boolean.opBoolean","INTERSECT",EDGE,{"disambiguationData":[OD(0.0)],"derivedFrom":[makeQuery(id+"F15.opRevolve","SWEPT_FACE",FACE,{"disambiguationData":[OSD([sQuery(id+"F14.wireOp",EDGE,"E75")])]}),makeQuery(id+"F25.opExtrude","SWEPT_FACE",FACE,{"disambiguationData":[OSD([sQuery(id+"F24.wireOp",EDGE,"E127")])]})]}),"instanceName":"4"});
            var Q26;
            {var subQ0=sQuery(id+"F14.wireOp",EDGE,"E74");var subQ1=sQuery(id+"F14.wireOp",EDGE,"E75");Q26=makeQuery(id+"F26.opPattern","SPLIT",EDGE,{"disambiguationData":[OD(5.0)],"derivedFrom":makeQuery(id+"F25.boolean.opBoolean","SPLIT",EDGE,{"disambiguationData":[TD([makeQuery(id+"F25.opExtrude","SWEPT_FACE",FACE,{"disambiguationData":[OSD([sQuery(id+"F24.wireOp",EDGE,"E127")])]})])],"derivedFrom":makeQuery(id+"F15.opRevolve","SWEPT_EDGE",EDGE,{"disambiguationData":[OSD([subQ0,subQ1])]})})});}
            var Q27;
            Q27=makeQuery(id+"F26.opPattern","COPY",EDGE,{"derivedFrom":makeQuery(id+"F25.boolean.opBoolean","INTERSECT",EDGE,{"disambiguationData":[OD(0.0)],"derivedFrom":[makeQuery(id+"F15.opRevolve","SWEPT_FACE",FACE,{"disambiguationData":[OSD([sQuery(id+"F14.wireOp",EDGE,"E75")])]}),makeQuery(id+"F25.opExtrude","SWEPT_FACE",FACE,{"disambiguationData":[OSD([sQuery(id+"F24.wireOp",EDGE,"E126")])]})]}),"instanceName":"5"});
            var Q28;
            Q28=makeQuery(id+"F26.opPattern","COPY",EDGE,{"derivedFrom":makeQuery(id+"F25.boolean.opBoolean","INTERSECT",EDGE,{"disambiguationData":[OD(0.0)],"derivedFrom":[makeQuery(id+"F15.opRevolve","SWEPT_FACE",FACE,{"disambiguationData":[OSD([sQuery(id+"F14.wireOp",EDGE,"E75")])]}),makeQuery(id+"F25.opExtrude","SWEPT_FACE",FACE,{"disambiguationData":[OSD([sQuery(id+"F24.wireOp",EDGE,"E127")])]})]}),"instanceName":"5"});
            var Q29;
            {var subQ0=sQuery(id+"F14.wireOp",EDGE,"E74");var subQ1=sQuery(id+"F14.wireOp",EDGE,"E75");Q29=makeQuery(id+"F26.opPattern","SPLIT",EDGE,{"disambiguationData":[OD(6.0)],"derivedFrom":makeQuery(id+"F25.boolean.opBoolean","SPLIT",EDGE,{"disambiguationData":[TD([makeQuery(id+"F25.opExtrude","SWEPT_FACE",FACE,{"disambiguationData":[OSD([sQuery(id+"F24.wireOp",EDGE,"E127")])]})])],"derivedFrom":makeQuery(id+"F15.opRevolve","SWEPT_EDGE",EDGE,{"disambiguationData":[OSD([subQ0,subQ1])]})})});}
            var Q30;
            Q30=makeQuery(id+"F26.opPattern","COPY",EDGE,{"derivedFrom":makeQuery(id+"F25.boolean.opBoolean","INTERSECT",EDGE,{"disambiguationData":[OD(0.0)],"derivedFrom":[makeQuery(id+"F15.opRevolve","SWEPT_FACE",FACE,{"disambiguationData":[OSD([sQuery(id+"F14.wireOp",EDGE,"E75")])]}),makeQuery(id+"F25.opExtrude","SWEPT_FACE",FACE,{"disambiguationData":[OSD([sQuery(id+"F24.wireOp",EDGE,"E126")])]})]}),"instanceName":"6"});
            var Q31;
            Q31=makeQuery(id+"F26.opPattern","COPY",EDGE,{"derivedFrom":makeQuery(id+"F25.boolean.opBoolean","INTERSECT",EDGE,{"disambiguationData":[OD(0.0)],"derivedFrom":[makeQuery(id+"F15.opRevolve","SWEPT_FACE",FACE,{"disambiguationData":[OSD([sQuery(id+"F14.wireOp",EDGE,"E75")])]}),makeQuery(id+"F25.opExtrude","SWEPT_FACE",FACE,{"disambiguationData":[OSD([sQuery(id+"F24.wireOp",EDGE,"E127")])]})]}),"instanceName":"6"});
            var Q32;
            {var subQ0=sQuery(id+"F14.wireOp",EDGE,"E74");var subQ1=sQuery(id+"F14.wireOp",EDGE,"E75");Q32=makeQuery(id+"F26.opPattern","SPLIT",EDGE,{"disambiguationData":[OD(7.0)],"derivedFrom":makeQuery(id+"F25.boolean.opBoolean","SPLIT",EDGE,{"disambiguationData":[TD([makeQuery(id+"F25.opExtrude","SWEPT_FACE",FACE,{"disambiguationData":[OSD([sQuery(id+"F24.wireOp",EDGE,"E127")])]})])],"derivedFrom":makeQuery(id+"F15.opRevolve","SWEPT_EDGE",EDGE,{"disambiguationData":[OSD([subQ0,subQ1])]})})});}
            var Q33;
            Q33=makeQuery(id+"F26.opPattern","COPY",EDGE,{"derivedFrom":makeQuery(id+"F25.boolean.opBoolean","INTERSECT",EDGE,{"disambiguationData":[OD(0.0)],"derivedFrom":[makeQuery(id+"F15.opRevolve","SWEPT_FACE",FACE,{"disambiguationData":[OSD([sQuery(id+"F14.wireOp",EDGE,"E75")])]}),makeQuery(id+"F25.opExtrude","SWEPT_FACE",FACE,{"disambiguationData":[OSD([sQuery(id+"F24.wireOp",EDGE,"E126")])]})]}),"instanceName":"7"});
            var Q34;
            Q34=makeQuery(id+"F26.opPattern","COPY",EDGE,{"derivedFrom":makeQuery(id+"F25.boolean.opBoolean","INTERSECT",EDGE,{"disambiguationData":[OD(0.0)],"derivedFrom":[makeQuery(id+"F15.opRevolve","SWEPT_FACE",FACE,{"disambiguationData":[OSD([sQuery(id+"F14.wireOp",EDGE,"E75")])]}),makeQuery(id+"F25.opExtrude","SWEPT_FACE",FACE,{"disambiguationData":[OSD([sQuery(id+"F24.wireOp",EDGE,"E127")])]})]}),"instanceName":"7"});
            var Q35;
            {var subQ0=sQuery(id+"F14.wireOp",EDGE,"E74");var subQ1=sQuery(id+"F14.wireOp",EDGE,"E75");Q35=makeQuery(id+"F26.opPattern","SPLIT",EDGE,{"disambiguationData":[OD(1.0)],"derivedFrom":makeQuery(id+"F25.boolean.opBoolean","SPLIT",EDGE,{"disambiguationData":[TD([makeQuery(id+"F25.opExtrude","SWEPT_FACE",FACE,{"disambiguationData":[OSD([sQuery(id+"F24.wireOp",EDGE,"E127")])]})])],"derivedFrom":makeQuery(id+"F15.opRevolve","SWEPT_EDGE",EDGE,{"disambiguationData":[OSD([subQ0,subQ1])]})})});}
            var Q36;
            Q36=makeQuery(id+"F25.boolean.opBoolean","INTERSECT",EDGE,{"disambiguationData":[OD(1.0)],"derivedFrom":[makeQuery(id+"F15.opRevolve","SWEPT_FACE",FACE,{"disambiguationData":[OSD([sQuery(id+"F14.wireOp",EDGE,"E75")])]}),makeQuery(id+"F25.opExtrude","SWEPT_FACE",FACE,{"disambiguationData":[OSD([sQuery(id+"F24.wireOp",EDGE,"E127")])]})]});
            var Q37;
            Q37=makeQuery(id+"F25.boolean.opBoolean","INTERSECT",EDGE,{"disambiguationData":[OD(1.0)],"derivedFrom":[makeQuery(id+"F15.opRevolve","SWEPT_FACE",FACE,{"disambiguationData":[OSD([sQuery(id+"F14.wireOp",EDGE,"E75")])]}),makeQuery(id+"F25.opExtrude","SWEPT_FACE",FACE,{"disambiguationData":[OSD([sQuery(id+"F24.wireOp",EDGE,"E126")])]})]});
            var Q38;
            {var subQ0=sQuery(id+"F14.wireOp",EDGE,"E74");var subQ1=sQuery(id+"F14.wireOp",EDGE,"E75");Q38=makeQuery(id+"F26.opPattern","SPLIT",EDGE,{"disambiguationData":[OD(1.0)],"derivedFrom":makeQuery(id+"F25.boolean.opBoolean","SPLIT",EDGE,{"disambiguationData":[TD([makeQuery(id+"F25.opExtrude","SWEPT_FACE",FACE,{"disambiguationData":[OSD([sQuery(id+"F24.wireOp",EDGE,"E126")])]})])],"derivedFrom":makeQuery(id+"F15.opRevolve","SWEPT_EDGE",EDGE,{"disambiguationData":[OSD([subQ0,subQ1])]})})});}
            var Q39;
            Q39=makeQuery(id+"F26.opPattern","COPY",EDGE,{"derivedFrom":makeQuery(id+"F25.boolean.opBoolean","INTERSECT",EDGE,{"disambiguationData":[OD(1.0)],"derivedFrom":[makeQuery(id+"F15.opRevolve","SWEPT_FACE",FACE,{"disambiguationData":[OSD([sQuery(id+"F14.wireOp",EDGE,"E75")])]}),makeQuery(id+"F25.opExtrude","SWEPT_FACE",FACE,{"disambiguationData":[OSD([sQuery(id+"F24.wireOp",EDGE,"E127")])]})]}),"instanceName":"1"});
            var Q40;
            Q40=makeQuery(id+"F26.opPattern","COPY",EDGE,{"derivedFrom":makeQuery(id+"F25.boolean.opBoolean","INTERSECT",EDGE,{"disambiguationData":[OD(1.0)],"derivedFrom":[makeQuery(id+"F15.opRevolve","SWEPT_FACE",FACE,{"disambiguationData":[OSD([sQuery(id+"F14.wireOp",EDGE,"E75")])]}),makeQuery(id+"F25.opExtrude","SWEPT_FACE",FACE,{"disambiguationData":[OSD([sQuery(id+"F24.wireOp",EDGE,"E126")])]})]}),"instanceName":"1"});
            var Q41;
            {var subQ0=sQuery(id+"F14.wireOp",EDGE,"E74");var subQ1=sQuery(id+"F14.wireOp",EDGE,"E75");Q41=makeQuery(id+"F26.opPattern","SPLIT",EDGE,{"disambiguationData":[OD(2.0)],"derivedFrom":makeQuery(id+"F25.boolean.opBoolean","SPLIT",EDGE,{"disambiguationData":[TD([makeQuery(id+"F25.opExtrude","SWEPT_FACE",FACE,{"disambiguationData":[OSD([sQuery(id+"F24.wireOp",EDGE,"E126")])]})])],"derivedFrom":makeQuery(id+"F15.opRevolve","SWEPT_EDGE",EDGE,{"disambiguationData":[OSD([subQ0,subQ1])]})})});}
            var Q42;
            Q42=makeQuery(id+"F26.opPattern","COPY",EDGE,{"derivedFrom":makeQuery(id+"F25.boolean.opBoolean","INTERSECT",EDGE,{"disambiguationData":[OD(1.0)],"derivedFrom":[makeQuery(id+"F15.opRevolve","SWEPT_FACE",FACE,{"disambiguationData":[OSD([sQuery(id+"F14.wireOp",EDGE,"E75")])]}),makeQuery(id+"F25.opExtrude","SWEPT_FACE",FACE,{"disambiguationData":[OSD([sQuery(id+"F24.wireOp",EDGE,"E127")])]})]}),"instanceName":"2"});
            var Q43;
            Q43=makeQuery(id+"F26.opPattern","COPY",EDGE,{"derivedFrom":makeQuery(id+"F25.boolean.opBoolean","INTERSECT",EDGE,{"disambiguationData":[OD(1.0)],"derivedFrom":[makeQuery(id+"F15.opRevolve","SWEPT_FACE",FACE,{"disambiguationData":[OSD([sQuery(id+"F14.wireOp",EDGE,"E75")])]}),makeQuery(id+"F25.opExtrude","SWEPT_FACE",FACE,{"disambiguationData":[OSD([sQuery(id+"F24.wireOp",EDGE,"E126")])]})]}),"instanceName":"2"});
            var Q44;
            {var subQ0=sQuery(id+"F14.wireOp",EDGE,"E74");var subQ1=sQuery(id+"F14.wireOp",EDGE,"E75");Q44=makeQuery(id+"F26.opPattern","SPLIT",EDGE,{"disambiguationData":[OD(3.0)],"derivedFrom":makeQuery(id+"F25.boolean.opBoolean","SPLIT",EDGE,{"disambiguationData":[TD([makeQuery(id+"F25.opExtrude","SWEPT_FACE",FACE,{"disambiguationData":[OSD([sQuery(id+"F24.wireOp",EDGE,"E126")])]})])],"derivedFrom":makeQuery(id+"F15.opRevolve","SWEPT_EDGE",EDGE,{"disambiguationData":[OSD([subQ0,subQ1])]})})});}
            var Q45;
            Q45=makeQuery(id+"F26.opPattern","COPY",EDGE,{"derivedFrom":makeQuery(id+"F25.boolean.opBoolean","INTERSECT",EDGE,{"disambiguationData":[OD(1.0)],"derivedFrom":[makeQuery(id+"F15.opRevolve","SWEPT_FACE",FACE,{"disambiguationData":[OSD([sQuery(id+"F14.wireOp",EDGE,"E75")])]}),makeQuery(id+"F25.opExtrude","SWEPT_FACE",FACE,{"disambiguationData":[OSD([sQuery(id+"F24.wireOp",EDGE,"E127")])]})]}),"instanceName":"3"});
            var Q46;
            Q46=makeQuery(id+"F26.opPattern","COPY",EDGE,{"derivedFrom":makeQuery(id+"F25.boolean.opBoolean","INTERSECT",EDGE,{"disambiguationData":[OD(1.0)],"derivedFrom":[makeQuery(id+"F15.opRevolve","SWEPT_FACE",FACE,{"disambiguationData":[OSD([sQuery(id+"F14.wireOp",EDGE,"E75")])]}),makeQuery(id+"F25.opExtrude","SWEPT_FACE",FACE,{"disambiguationData":[OSD([sQuery(id+"F24.wireOp",EDGE,"E126")])]})]}),"instanceName":"3"});
            var Q47;
            {var subQ0=sQuery(id+"F14.wireOp",EDGE,"E74");var subQ1=sQuery(id+"F14.wireOp",EDGE,"E75");Q47=makeQuery(id+"F26.opPattern","SPLIT",EDGE,{"disambiguationData":[OD(4.0)],"derivedFrom":makeQuery(id+"F25.boolean.opBoolean","SPLIT",EDGE,{"disambiguationData":[TD([makeQuery(id+"F25.opExtrude","SWEPT_FACE",FACE,{"disambiguationData":[OSD([sQuery(id+"F24.wireOp",EDGE,"E126")])]})])],"derivedFrom":makeQuery(id+"F15.opRevolve","SWEPT_EDGE",EDGE,{"disambiguationData":[OSD([subQ0,subQ1])]})})});}
            fillet(context, id + "F28", {"entities" : qUnion([Q0, Q1, Q2, Q3, Q4, Q5, Q6, Q7, Q8, Q9, Q10, Q11, Q12, Q13, Q14, Q15, Q16, Q17, Q18, Q19, Q20, Q21, Q22, Q23, Q24, Q25, Q26, Q27, Q28, Q29, Q30, Q31, Q32, Q33, Q34, Q35, Q36, Q37, Q38, Q39, Q40, Q41, Q42, Q43, Q44, Q45, Q46, Q47]), "radius" : 0.5 * mm, "tangentPropagation" : true, "allowEdgeOverflow" : false});
        }
    });
